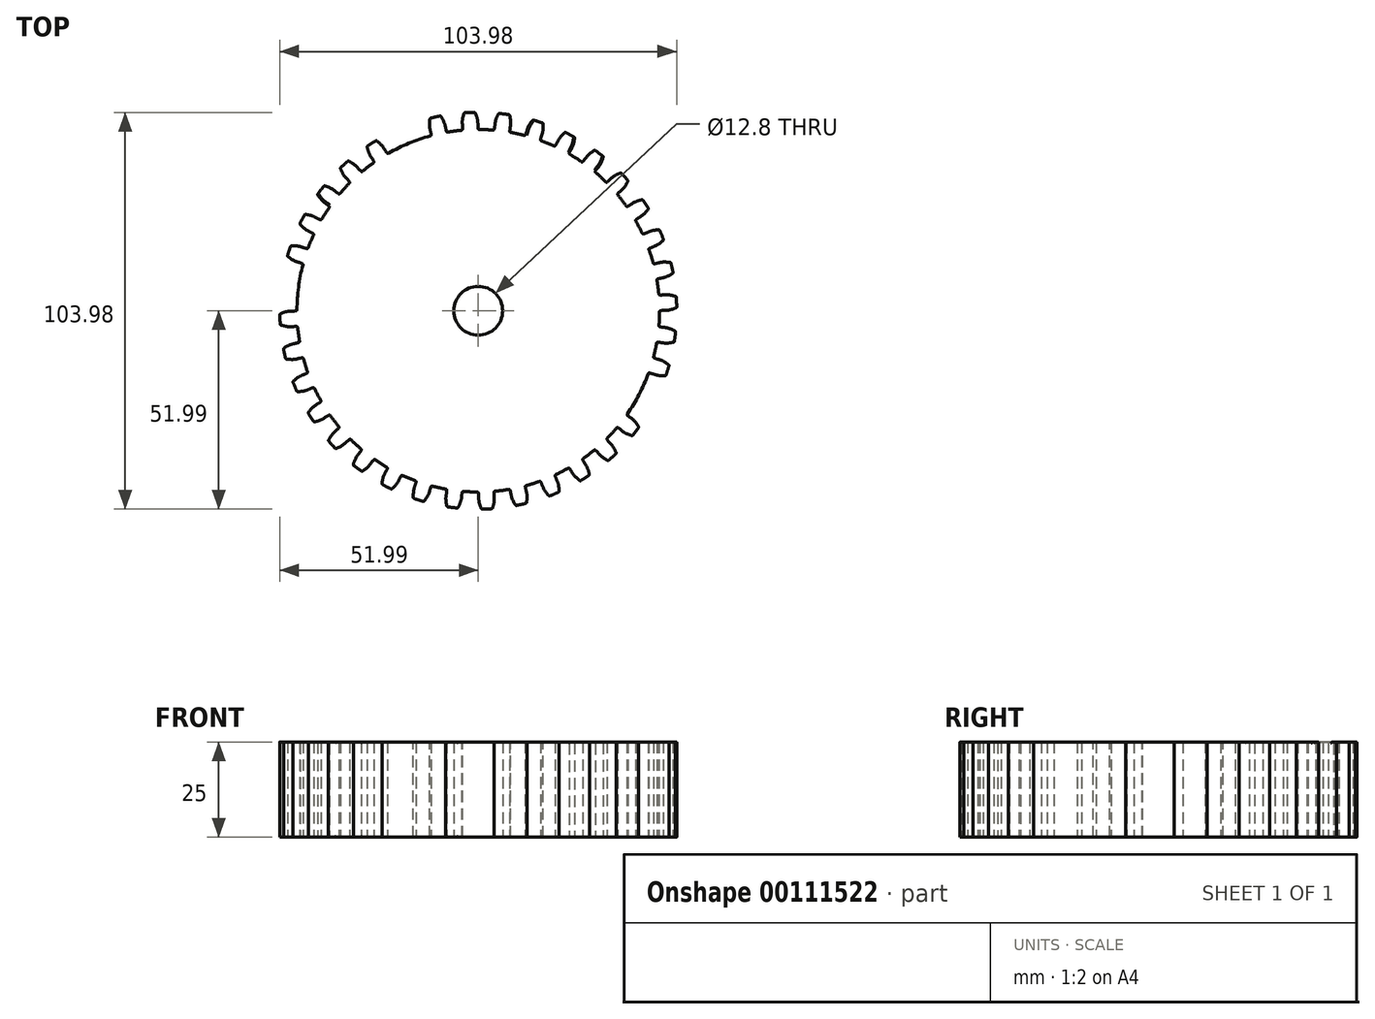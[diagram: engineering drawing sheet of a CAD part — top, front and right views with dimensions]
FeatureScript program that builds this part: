
annotation { "Feature Type Name" : "Feature", "Feature Type Description" : "" }
export const myFeature = defineFeature(function(context is Context, id is Id, definition is map)
    precondition{}
    {
        {
            var Q0;
            Q0=qCreatedBy(makeId("Top.planeOp"),FACE);
            var sketch = newSketch(context, id + "F0", { "sketchPlane" : qUnion([Q0])});
            skCircle(sketch, "E0", {"center": v(0, 0) * mm, "radius": 47.5 * mm});
            skCircle(sketch, "E1", {"center": v(0, 0) * mm, "radius": 52 * mm});
            skFitSpline(sketch, "E2", {"points": [v(-0.54, 52) * mm, v(0, 50) * mm, v(0.28, 47.5) * mm], "startDerivative": vector(1.25, -3.55) * mm, "endDerivative": vector(0.53, -5.13) * mm});
            skFitSpline(sketch, "E3.MirrorCS", {"points": [v(0.54, 52) * mm, v(0, 50) * mm, v(-0.28, 47.5) * mm], "startDerivative": vector(-1.25, -3.55) * mm, "endDerivative": vector(-0.53, -5.13) * mm});
            skFitSpline(sketch, "E4.0", {"points": [v(-0.54, 52) * mm, v(-0.34, 51.43) * mm, v(0.1, 49.94) * mm, v(0.19, 48.4) * mm, v(0.28, 47.5) * mm]});
            skFitSpline(sketch, "E5.0", {"points": [v(-0.82, 52) * mm, v(-0.62, 51.44) * mm, v(-0.18, 49.94) * mm, v(-0.1, 48.4) * mm, v(0, 47.5) * mm]});
            skCircle(sketch, "E6.3.0", {"center": v(0, 0) * mm, "radius": 73.48 * mm});
            skCircle(sketch, "E6.4.0", {"center": v(0, 0) * mm, "radius": 73.48 * mm});
            skCircle(sketch, "E6.6.0", {"center": v(0, 0) * mm, "radius": 73.48 * mm});
            skCircle(sketch, "E6.7.0", {"center": v(0, 0) * mm, "radius": 73.48 * mm});
            skCircle(sketch, "E6.8.0", {"center": v(0, 0) * mm, "radius": 73.48 * mm});
            skCircle(sketch, "E6.9.0", {"center": v(0, 0) * mm, "radius": 73.48 * mm});
            skCircle(sketch, "E6.10.0", {"center": v(0, 0) * mm, "radius": 73.48 * mm});
            skCircle(sketch, "E6.11.0", {"center": v(0, 0) * mm, "radius": 73.48 * mm});
            skCircle(sketch, "E6.12.0", {"center": v(0, 0) * mm, "radius": 73.48 * mm});
            skCircle(sketch, "E6.13.0", {"center": v(0, 0) * mm, "radius": 73.48 * mm});
            skCircle(sketch, "E6.14.0", {"center": v(0, 0) * mm, "radius": 73.48 * mm});
            skCircle(sketch, "E6.15.0", {"center": v(0, 0) * mm, "radius": 73.48 * mm});
            skCircle(sketch, "E6.16.0", {"center": v(0, 0) * mm, "radius": 73.48 * mm});
            skCircle(sketch, "E6.17.0", {"center": v(0, 0) * mm, "radius": 73.48 * mm});
            skCircle(sketch, "E6.18.0", {"center": v(0, 0) * mm, "radius": 73.48 * mm});
            skCircle(sketch, "E6.19.0", {"center": v(0, 0) * mm, "radius": 73.48 * mm});
            skCircle(sketch, "E6.20.0", {"center": v(0, 0) * mm, "radius": 73.48 * mm});
            skCircle(sketch, "E6.21.0", {"center": v(0, 0) * mm, "radius": 73.48 * mm});
            skCircle(sketch, "E6.22.0", {"center": v(0, 0) * mm, "radius": 73.48 * mm});
            skCircle(sketch, "E6.23.0", {"center": v(0, 0) * mm, "radius": 73.48 * mm});
            skCircle(sketch, "E6.24.0", {"center": v(0, 0) * mm, "radius": 73.48 * mm});
            skCircle(sketch, "E6.26.0", {"center": v(0, 0) * mm, "radius": 73.48 * mm});
            skCircle(sketch, "E6.27.0", {"center": v(0, 0) * mm, "radius": 73.48 * mm});
            skCircle(sketch, "E6.28.0", {"center": v(0, 0) * mm, "radius": 73.48 * mm});
            skCircle(sketch, "E6.29.0", {"center": v(0, 0) * mm, "radius": 73.48 * mm});
            skCircle(sketch, "E6.30.0", {"center": v(0, 0) * mm, "radius": 73.48 * mm});
            skCircle(sketch, "E6.31.0", {"center": v(0, 0) * mm, "radius": 73.48 * mm});
            skCircle(sketch, "E6.32.0", {"center": v(0, 0) * mm, "radius": 73.48 * mm});
            skCircle(sketch, "E6.33.0", {"center": v(0, 0) * mm, "radius": 73.48 * mm});
            skCircle(sketch, "E6.34.0", {"center": v(0, 0) * mm, "radius": 73.48 * mm});
            skCircle(sketch, "E6.35.0", {"center": v(0, 0) * mm, "radius": 73.48 * mm});
            skCircle(sketch, "E6.36.0", {"center": v(0, 0) * mm, "radius": 73.48 * mm});
            skCircle(sketch, "E6.38.0", {"center": v(0, 0) * mm, "radius": 73.48 * mm});
            skCircle(sketch, "E6.39.0", {"center": v(0, 0) * mm, "radius": 73.48 * mm});
            skCircle(sketch, "E6.40.0", {"center": v(0, 0) * mm, "radius": 73.48 * mm});
            skCircle(sketch, "E6.41.0", {"center": v(0, 0) * mm, "radius": 73.48 * mm});
            skCircle(sketch, "E6.42.0", {"center": v(0, 0) * mm, "radius": 73.48 * mm});
            skCircle(sketch, "E6.43.0", {"center": v(0, 0) * mm, "radius": 73.48 * mm});
            skCircle(sketch, "E6.44.0", {"center": v(0, 0) * mm, "radius": 73.48 * mm});
            skCircle(sketch, "E6.45.0", {"center": v(0, 0) * mm, "radius": 73.48 * mm});
            skCircle(sketch, "E6.46.0", {"center": v(0, 0) * mm, "radius": 73.48 * mm});
            skCircle(sketch, "E6.47.0", {"center": v(0, 0) * mm, "radius": 73.48 * mm});
            skCircle(sketch, "E6.49.0", {"center": v(0, 0) * mm, "radius": 73.48 * mm});
            skCircle(sketch, "E6.50.0", {"center": v(0, 0) * mm, "radius": 73.48 * mm});
            skCircle(sketch, "E6.52.0", {"center": v(0, 0) * mm, "radius": 73.48 * mm});
            skCircle(sketch, "E6.53.0", {"center": v(0, 0) * mm, "radius": 73.48 * mm});
            skCircle(sketch, "E6.54.0", {"center": v(0, 0) * mm, "radius": 73.48 * mm});
            skCircle(sketch, "E6.55.0", {"center": v(0, 0) * mm, "radius": 73.48 * mm});
            skCircle(sketch, "E6.56.0", {"center": v(0, 0) * mm, "radius": 73.48 * mm});
            skCircle(sketch, "E6.57.0", {"center": v(0, 0) * mm, "radius": 73.48 * mm});
            skCircle(sketch, "E6.58.0", {"center": v(0, 0) * mm, "radius": 73.48 * mm});
            skCircle(sketch, "E6.59.0", {"center": v(0, 0) * mm, "radius": 73.48 * mm});
            skCircle(sketch, "E6.60.0", {"center": v(0, 0) * mm, "radius": 73.48 * mm});
            skCircle(sketch, "E6.61.0", {"center": v(0, 0) * mm, "radius": 73.48 * mm});
            skCircle(sketch, "E6.62.0", {"center": v(0, 0) * mm, "radius": 73.48 * mm});
            skCircle(sketch, "E6.63.0", {"center": v(0, 0) * mm, "radius": 73.48 * mm});
            skCircle(sketch, "E6.64.0", {"center": v(0, 0) * mm, "radius": 73.48 * mm});
            skCircle(sketch, "E6.65.0", {"center": v(0, 0) * mm, "radius": 73.48 * mm});
            skCircle(sketch, "E6.66.0", {"center": v(0, 0) * mm, "radius": 73.48 * mm});
            skCircle(sketch, "E6.67.0", {"center": v(0, 0) * mm, "radius": 73.48 * mm});
            skCircle(sketch, "E6.68.0", {"center": v(0, 0) * mm, "radius": 73.48 * mm});
            skCircle(sketch, "E6.69.0", {"center": v(0, 0) * mm, "radius": 73.48 * mm});
            skCircle(sketch, "E6.70.0", {"center": v(0, 0) * mm, "radius": 73.48 * mm});
            skCircle(sketch, "E6.71.0", {"center": v(0, 0) * mm, "radius": 73.48 * mm});
            skCircle(sketch, "E6.72.0", {"center": v(0, 0) * mm, "radius": 73.48 * mm});
            skCircle(sketch, "E6.73.0", {"center": v(0, 0) * mm, "radius": 73.48 * mm});
            skCircle(sketch, "E6.74.0", {"center": v(0, 0) * mm, "radius": 73.48 * mm});
            skCircle(sketch, "E6.75.0", {"center": v(0, 0) * mm, "radius": 73.48 * mm});
            skCircle(sketch, "E6.76.0", {"center": v(0, 0) * mm, "radius": 73.48 * mm});
            skCircle(sketch, "E6.77.0", {"center": v(0, 0) * mm, "radius": 73.48 * mm});
            skCircle(sketch, "E6.78.0", {"center": v(0, 0) * mm, "radius": 73.48 * mm});
            skCircle(sketch, "E6.79.0", {"center": v(0, 0) * mm, "radius": 73.48 * mm});
            skCircle(sketch, "E6.80.0", {"center": v(0, 0) * mm, "radius": 73.48 * mm});
            skCircle(sketch, "E6.81.0", {"center": v(0, 0) * mm, "radius": 73.48 * mm});
            skCircle(sketch, "E6.82.0", {"center": v(0, 0) * mm, "radius": 73.48 * mm});
            skCircle(sketch, "E6.83.0", {"center": v(0, 0) * mm, "radius": 73.48 * mm});
            skCircle(sketch, "E6.84.0", {"center": v(0, 0) * mm, "radius": 73.48 * mm});
            skCircle(sketch, "E6.85.0", {"center": v(0, 0) * mm, "radius": 73.48 * mm});
            skCircle(sketch, "E6.86.0", {"center": v(0, 0) * mm, "radius": 73.48 * mm});
            skCircle(sketch, "E6.87.0", {"center": v(0, 0) * mm, "radius": 73.48 * mm});
            skCircle(sketch, "E6.88.0", {"center": v(0, 0) * mm, "radius": 73.48 * mm});
            skCircle(sketch, "E6.89.0", {"center": v(0, 0) * mm, "radius": 73.48 * mm});
            skCircle(sketch, "E6.90.0", {"center": v(0, 0) * mm, "radius": 73.48 * mm});
            skCircle(sketch, "E6.91.0", {"center": v(0, 0) * mm, "radius": 73.48 * mm});
            skCircle(sketch, "E6.92.0", {"center": v(0, 0) * mm, "radius": 73.48 * mm});
            skCircle(sketch, "E6.93.0", {"center": v(0, 0) * mm, "radius": 73.48 * mm});
            skCircle(sketch, "E6.94.0", {"center": v(0, 0) * mm, "radius": 73.48 * mm});
            skCircle(sketch, "E6.95.0", {"center": v(0, 0) * mm, "radius": 73.48 * mm});
            skCircle(sketch, "E6.96.0", {"center": v(0, 0) * mm, "radius": 73.48 * mm});
            skCircle(sketch, "E6.97.0", {"center": v(0, 0) * mm, "radius": 73.48 * mm});
            skCircle(sketch, "E6.98.0", {"center": v(0, 0) * mm, "radius": 73.48 * mm});
            skCircle(sketch, "E6.99.0", {"center": v(0, 0) * mm, "radius": 73.48 * mm});
            skCircle(sketch, "E6.100.0", {"center": v(0, 0) * mm, "radius": 73.48 * mm});
            skCircle(sketch, "E6.101.0", {"center": v(0, 0) * mm, "radius": 73.48 * mm});
            skCircle(sketch, "E6.102.0", {"center": v(0, 0) * mm, "radius": 73.48 * mm});
            skCircle(sketch, "E6.103.0", {"center": v(0, 0) * mm, "radius": 73.48 * mm});
            skCircle(sketch, "E6.104.0", {"center": v(0, 0) * mm, "radius": 73.48 * mm});
            skCircle(sketch, "E6.105.0", {"center": v(0, 0) * mm, "radius": 73.48 * mm});
            skCircle(sketch, "E6.106.0", {"center": v(0, 0) * mm, "radius": 73.48 * mm});
            skCircle(sketch, "E6.109.0", {"center": v(0, 0) * mm, "radius": 73.48 * mm});
            skCircle(sketch, "E6.113.0", {"center": v(0, 0) * mm, "radius": 73.48 * mm});
            skCircle(sketch, "E6.114.0", {"center": v(0, 0) * mm, "radius": 73.48 * mm});
            skCircle(sketch, "E6.115.0", {"center": v(0, 0) * mm, "radius": 73.48 * mm});
            skCircle(sketch, "E6.116.0", {"center": v(0, 0) * mm, "radius": 73.48 * mm});
            skCircle(sketch, "E6.117.0", {"center": v(0, 0) * mm, "radius": 73.48 * mm});
            skCircle(sketch, "E6.118.0", {"center": v(0, 0) * mm, "radius": 73.48 * mm});
            skCircle(sketch, "E6.119.0", {"center": v(0, 0) * mm, "radius": 73.48 * mm});
            skCircle(sketch, "E6.120.0", {"center": v(0, 0) * mm, "radius": 73.48 * mm});
            skCircle(sketch, "E6.123.0", {"center": v(0, 0) * mm, "radius": 73.48 * mm});
            skCircle(sketch, "E6.124.0", {"center": v(0, 0) * mm, "radius": 73.48 * mm});
            skCircle(sketch, "E6.125.0", {"center": v(0, 0) * mm, "radius": 73.48 * mm});
            skCircle(sketch, "E6.126.0", {"center": v(0, 0) * mm, "radius": 73.48 * mm});
            skCircle(sketch, "E6.127.0", {"center": v(0, 0) * mm, "radius": 73.48 * mm});
            skCircle(sketch, "E6.128.0", {"center": v(0, 0) * mm, "radius": 73.48 * mm});
            skCircle(sketch, "E6.130.0", {"center": v(0, 0) * mm, "radius": 73.48 * mm});
            skCircle(sketch, "E6.134.0", {"center": v(0, 0) * mm, "radius": 73.48 * mm});
            skCircle(sketch, "E6.135.0", {"center": v(0, 0) * mm, "radius": 73.48 * mm});
            skCircle(sketch, "E6.137.0", {"center": v(0, 0) * mm, "radius": 73.48 * mm});
            skCircle(sketch, "E6.138.0", {"center": v(0, 0) * mm, "radius": 73.48 * mm});
            skCircle(sketch, "E6.139.0", {"center": v(0, 0) * mm, "radius": 73.48 * mm});
            skCircle(sketch, "E6.140.0", {"center": v(0, 0) * mm, "radius": 73.48 * mm});
            skCircle(sketch, "E6.141.0", {"center": v(0, 0) * mm, "radius": 73.48 * mm});
            skCircle(sketch, "E6.142.0", {"center": v(0, 0) * mm, "radius": 73.48 * mm});
            skCircle(sketch, "E6.143.0", {"center": v(0, 0) * mm, "radius": 73.48 * mm});
            skFitSpline(sketch, "E7.MirrorCS", {"points": [v(-3.72, 51.87) * mm, v(-3.86, 51.3) * mm, v(-4.18, 49.76) * mm, v(-4.13, 48.22) * mm, v(-4.14, 47.32) * mm]});
            skFitSpline(sketch, "E8.MirrorCS", {"points": [v(-3.72, 51.87) * mm, v(-3.86, 51.3) * mm, v(-4.18, 49.76) * mm, v(-4.13, 48.22) * mm, v(-4.14, 47.32) * mm]});
            skFitSpline(sketch, "E9.MirrorCS", {"points": [v(-3.72, 51.87) * mm, v(-3.86, 51.3) * mm, v(-4.18, 49.76) * mm, v(-4.13, 48.22) * mm, v(-4.14, 47.32) * mm]});
            skFitSpline(sketch, "E10.MirrorCS", {"points": [v(-3.72, 51.87) * mm, v(-3.86, 51.3) * mm, v(-4.18, 49.76) * mm, v(-4.13, 48.22) * mm, v(-4.14, 47.32) * mm]});
            skFitSpline(sketch, "E11.MirrorCS", {"points": [v(-9.84, 51.07) * mm, v(-9.54, 50.55) * mm, v(-8.85, 49.15) * mm, v(-8.5, 47.64) * mm, v(-8.25, 46.78) * mm]});
            skFitSpline(sketch, "E12.MirrorCS", {"points": [v(-12.67, 50.44) * mm, v(-12.71, 49.84) * mm, v(-12.75, 48.28) * mm, v(-12.44, 46.77) * mm, v(-12.3, 45.88) * mm]});
            skFitSpline(sketch, "E13.MirrorCS", {"points": [v(-18.55, 48.58) * mm, v(-18.18, 48.12) * mm, v(-17.25, 46.86) * mm, v(-16.64, 45.45) * mm, v(-16.25, 44.64) * mm]});
            skFitSpline(sketch, "E14.MirrorCS", {"points": [v(-18.55, 48.58) * mm, v(-18.18, 48.12) * mm, v(-17.25, 46.86) * mm, v(-16.64, 45.45) * mm, v(-16.25, 44.64) * mm]});
            skFitSpline(sketch, "E15.MirrorCS", {"points": [v(-21.23, 47.47) * mm, v(-21.17, 46.88) * mm, v(-20.94, 45.33) * mm, v(-20.37, 43.9) * mm, v(-20.07, 43.05) * mm]});
            skFitSpline(sketch, "E16.MirrorCS", {"points": [v(-26.7, 44.62) * mm, v(-26.26, 44.23) * mm, v(-25.12, 43.16) * mm, v(-24.28, 41.87) * mm, v(-23.75, 41.14) * mm]});
            skFitSpline(sketch, "E17.MirrorCS", {"points": [v(-29.15, 43.06) * mm, v(-29, 42.5) * mm, v(-28.5, 41) * mm, v(-27.68, 39.7) * mm, v(-27.24, 38.91) * mm]});
            skFitSpline(sketch, "E18.MirrorCS", {"points": [v(-34.05, 39.3) * mm, v(-33.54, 39) * mm, v(-32.23, 38.14) * mm, v(-31.18, 37.01) * mm, v(-30.53, 36.39) * mm]});
            skFitSpline(sketch, "E19.MirrorCS", {"points": [v(-36.19, 37.35) * mm, v(-35.93, 36.81) * mm, v(-35.19, 35.44) * mm, v(-34.16, 34.29) * mm, v(-33.59, 33.59) * mm]});
            skFitSpline(sketch, "E20.MirrorCS", {"points": [v(-40.36, 32.8) * mm, v(-39.8, 32.59) * mm, v(-38.37, 31.96) * mm, v(-37.13, 31.04) * mm, v(-36.39, 30.53) * mm]});
            skFitSpline(sketch, "E21.MirrorCS", {"points": [v(-42.12, 30.5) * mm, v(-41.78, 30.01) * mm, v(-40.8, 28.79) * mm, v(-39.6, 27.83) * mm, v(-38.9, 27.25) * mm]});
            skFitSpline(sketch, "E22.MirrorCS", {"points": [v(-45.44, 25.29) * mm, v(-44.86, 25.18) * mm, v(-43.34, 24.81) * mm, v(-41.96, 24.12) * mm, v(-41.14, 23.75) * mm]});
            skFitSpline(sketch, "E23.MirrorCS", {"points": [v(-46.78, 22.72) * mm, v(-46.35, 22.3) * mm, v(-45.18, 21.26) * mm, v(-43.82, 20.54) * mm, v(-43.05, 20.08) * mm]});
            skFitSpline(sketch, "E24.MirrorCS", {"points": [v(-49.14, 17.01) * mm, v(-48.55, 17) * mm, v(-46.99, 16.91) * mm, v(-45.5, 16.47) * mm, v(-44.64, 16.25) * mm]});
            skFitSpline(sketch, "E25.MirrorCS", {"points": [v(-50.01, 14.25) * mm, v(-49.52, 13.91) * mm, v(-48.19, 13.1) * mm, v(-46.72, 12.62) * mm, v(-45.88, 12.3) * mm]});
            skFitSpline(sketch, "E26.MirrorCS", {"points": [v(-51.35, 8.22) * mm, v(-50.76, 8.32) * mm, v(-49.2, 8.5) * mm, v(-47.68, 8.31) * mm, v(-46.78, 8.25) * mm]});
            skFitSpline(sketch, "E27.MirrorCS", {"points": [v(-51.35, 8.22) * mm, v(-50.76, 8.32) * mm, v(-49.2, 8.5) * mm, v(-47.68, 8.31) * mm, v(-46.78, 8.25) * mm]});
            skFitSpline(sketch, "E28.MirrorCS", {"points": [v(-51.73, 5.35) * mm, v(-51.19, 5.1) * mm, v(-49.73, 4.53) * mm, v(-48.2, 4.31) * mm, v(-47.32, 4.14) * mm]});
            skFitSpline(sketch, "E29.MirrorCS", {"points": [v(-52, -0.82) * mm, v(-51.44, -0.62) * mm, v(-49.94, -0.18) * mm, v(-48.4, -0.1) * mm, v(-47.5, 0) * mm]});
            skFitSpline(sketch, "E30.MirrorCS", {"points": [v(-51.87, -3.72) * mm, v(-51.3, -3.86) * mm, v(-49.76, -4.18) * mm, v(-48.22, -4.13) * mm, v(-47.32, -4.14) * mm]});
            skFitSpline(sketch, "E31.MirrorCS", {"points": [v(-51.07, -9.84) * mm, v(-50.55, -9.54) * mm, v(-49.15, -8.85) * mm, v(-47.64, -8.5) * mm, v(-46.78, -8.25) * mm]});
            skFitSpline(sketch, "E32.MirrorCS", {"points": [v(-50.44, -12.67) * mm, v(-49.84, -12.71) * mm, v(-48.28, -12.75) * mm, v(-46.77, -12.44) * mm, v(-45.88, -12.3) * mm]});
            skFitSpline(sketch, "E33.MirrorCS", {"points": [v(-48.58, -18.55) * mm, v(-48.12, -18.18) * mm, v(-46.86, -17.25) * mm, v(-45.45, -16.64) * mm, v(-44.64, -16.25) * mm]});
            skFitSpline(sketch, "E34.MirrorCS", {"points": [v(-47.47, -21.23) * mm, v(-46.88, -21.17) * mm, v(-45.33, -20.94) * mm, v(-43.9, -20.37) * mm, v(-43.05, -20.07) * mm]});
            skFitSpline(sketch, "E35.MirrorCS", {"points": [v(-44.62, -26.7) * mm, v(-44.23, -26.26) * mm, v(-43.16, -25.12) * mm, v(-41.87, -24.28) * mm, v(-41.14, -23.75) * mm]});
            skFitSpline(sketch, "E36.MirrorCS", {"points": [v(-43.06, -29.15) * mm, v(-42.5, -29) * mm, v(-41, -28.5) * mm, v(-39.7, -27.68) * mm, v(-38.91, -27.24) * mm]});
            skFitSpline(sketch, "E37.MirrorCS", {"points": [v(-39.3, -34.05) * mm, v(-39, -33.54) * mm, v(-38.14, -32.23) * mm, v(-37.01, -31.18) * mm, v(-36.39, -30.53) * mm]});
            skFitSpline(sketch, "E38.MirrorCS", {"points": [v(-37.35, -36.19) * mm, v(-36.81, -35.93) * mm, v(-35.44, -35.19) * mm, v(-34.29, -34.16) * mm, v(-33.59, -33.59) * mm]});
            skFitSpline(sketch, "E39.MirrorCS", {"points": [v(-32.8, -40.36) * mm, v(-32.59, -39.8) * mm, v(-31.96, -38.37) * mm, v(-31.04, -37.13) * mm, v(-30.53, -36.39) * mm]});
            skFitSpline(sketch, "E40.MirrorCS", {"points": [v(-30.5, -42.12) * mm, v(-30.01, -41.78) * mm, v(-28.79, -40.8) * mm, v(-27.83, -39.6) * mm, v(-27.25, -38.9) * mm]});
            skFitSpline(sketch, "E41.MirrorCS", {"points": [v(-25.29, -45.44) * mm, v(-25.18, -44.86) * mm, v(-24.81, -43.34) * mm, v(-24.12, -41.96) * mm, v(-23.75, -41.14) * mm]});
            skFitSpline(sketch, "E42.MirrorCS", {"points": [v(-22.72, -46.78) * mm, v(-22.3, -46.35) * mm, v(-21.26, -45.18) * mm, v(-20.54, -43.82) * mm, v(-20.08, -43.05) * mm]});
            skFitSpline(sketch, "E43.MirrorCS", {"points": [v(-17.01, -49.14) * mm, v(-17, -48.55) * mm, v(-16.91, -46.99) * mm, v(-16.47, -45.5) * mm, v(-16.25, -44.64) * mm]});
            skFitSpline(sketch, "E44.MirrorCS", {"points": [v(-14.25, -50.01) * mm, v(-13.91, -49.52) * mm, v(-13.1, -48.19) * mm, v(-12.62, -46.72) * mm, v(-12.3, -45.88) * mm]});
            skFitSpline(sketch, "E45.MirrorCS", {"points": [v(-8.22, -51.35) * mm, v(-8.32, -50.76) * mm, v(-8.5, -49.2) * mm, v(-8.31, -47.68) * mm, v(-8.25, -46.78) * mm]});
            skFitSpline(sketch, "E46.MirrorCS", {"points": [v(-5.35, -51.73) * mm, v(-5.1, -51.19) * mm, v(-4.53, -49.73) * mm, v(-4.31, -48.2) * mm, v(-4.14, -47.32) * mm]});
            skFitSpline(sketch, "E47.MirrorCS", {"points": [v(0.82, -52) * mm, v(0.62, -51.44) * mm, v(0.18, -49.94) * mm, v(0.1, -48.4) * mm, v(0, -47.5) * mm]});
            skFitSpline(sketch, "E48.MirrorCS", {"points": [v(3.72, -51.87) * mm, v(3.86, -51.3) * mm, v(4.18, -49.76) * mm, v(4.13, -48.22) * mm, v(4.14, -47.32) * mm]});
            skFitSpline(sketch, "E49.MirrorCS", {"points": [v(3.72, -51.87) * mm, v(3.86, -51.3) * mm, v(4.18, -49.76) * mm, v(4.13, -48.22) * mm, v(4.14, -47.32) * mm]});
            skFitSpline(sketch, "E50.MirrorCS", {"points": [v(9.84, -51.07) * mm, v(9.54, -50.55) * mm, v(8.85, -49.15) * mm, v(8.5, -47.64) * mm, v(8.25, -46.78) * mm]});
            skFitSpline(sketch, "E51.MirrorCS", {"points": [v(12.67, -50.44) * mm, v(12.71, -49.84) * mm, v(12.75, -48.28) * mm, v(12.44, -46.77) * mm, v(12.3, -45.88) * mm]});
            skFitSpline(sketch, "E52.MirrorCS", {"points": [v(18.55, -48.58) * mm, v(18.18, -48.12) * mm, v(17.25, -46.86) * mm, v(16.64, -45.45) * mm, v(16.25, -44.64) * mm]});
            skFitSpline(sketch, "E53.MirrorCS", {"points": [v(21.23, -47.47) * mm, v(21.17, -46.88) * mm, v(20.94, -45.33) * mm, v(20.37, -43.9) * mm, v(20.07, -43.05) * mm]});
            skFitSpline(sketch, "E54.MirrorCS", {"points": [v(26.7, -44.62) * mm, v(26.26, -44.23) * mm, v(25.12, -43.16) * mm, v(24.28, -41.87) * mm, v(23.75, -41.14) * mm]});
            skFitSpline(sketch, "E55.MirrorCS", {"points": [v(29.15, -43.06) * mm, v(29, -42.5) * mm, v(28.5, -41) * mm, v(27.68, -39.7) * mm, v(27.24, -38.91) * mm]});
            skFitSpline(sketch, "E56.MirrorCS", {"points": [v(34.05, -39.3) * mm, v(33.54, -39) * mm, v(32.23, -38.14) * mm, v(31.18, -37.01) * mm, v(30.53, -36.39) * mm]});
            skFitSpline(sketch, "E57.MirrorCS", {"points": [v(36.19, -37.35) * mm, v(35.93, -36.81) * mm, v(35.19, -35.44) * mm, v(34.16, -34.29) * mm, v(33.59, -33.59) * mm]});
            skFitSpline(sketch, "E58.MirrorCS", {"points": [v(40.36, -32.8) * mm, v(39.8, -32.59) * mm, v(38.37, -31.96) * mm, v(37.13, -31.04) * mm, v(36.39, -30.53) * mm]});
            skFitSpline(sketch, "E59.MirrorCS", {"points": [v(42.12, -30.5) * mm, v(41.78, -30.01) * mm, v(40.8, -28.79) * mm, v(39.6, -27.83) * mm, v(38.9, -27.25) * mm]});
            skFitSpline(sketch, "E60.MirrorCS", {"points": [v(45.44, -25.29) * mm, v(44.86, -25.18) * mm, v(43.34, -24.81) * mm, v(41.96, -24.12) * mm, v(41.14, -23.75) * mm]});
            skFitSpline(sketch, "E61.MirrorCS", {"points": [v(45.44, -25.29) * mm, v(44.86, -25.18) * mm, v(43.34, -24.81) * mm, v(41.96, -24.12) * mm, v(41.14, -23.75) * mm]});
            skFitSpline(sketch, "E62.MirrorCS", {"points": [v(46.78, -22.72) * mm, v(46.35, -22.3) * mm, v(45.18, -21.26) * mm, v(43.82, -20.54) * mm, v(43.05, -20.08) * mm]});
            skFitSpline(sketch, "E63.MirrorCS", {"points": [v(49.14, -17.01) * mm, v(48.55, -17) * mm, v(46.99, -16.91) * mm, v(45.5, -16.47) * mm, v(44.64, -16.25) * mm]});
            skFitSpline(sketch, "E64.MirrorCS", {"points": [v(50.01, -14.25) * mm, v(49.52, -13.91) * mm, v(48.19, -13.1) * mm, v(46.72, -12.62) * mm, v(45.88, -12.3) * mm]});
            skFitSpline(sketch, "E65.MirrorCS", {"points": [v(51.35, -8.22) * mm, v(50.76, -8.32) * mm, v(49.2, -8.5) * mm, v(47.68, -8.31) * mm, v(46.78, -8.25) * mm]});
            skFitSpline(sketch, "E66.MirrorCS", {"points": [v(51.73, -5.35) * mm, v(51.19, -5.1) * mm, v(49.73, -4.53) * mm, v(48.2, -4.31) * mm, v(47.32, -4.14) * mm]});
            skFitSpline(sketch, "E67.MirrorCS", {"points": [v(52, 0.82) * mm, v(51.44, 0.62) * mm, v(49.94, 0.18) * mm, v(48.4, 0.1) * mm, v(47.5, 0) * mm]});
            skFitSpline(sketch, "E68.MirrorCS", {"points": [v(51.87, 3.72) * mm, v(51.3, 3.86) * mm, v(49.76, 4.18) * mm, v(48.22, 4.13) * mm, v(47.32, 4.14) * mm]});
            skFitSpline(sketch, "E69.MirrorCS", {"points": [v(51.07, 9.84) * mm, v(50.55, 9.54) * mm, v(49.15, 8.85) * mm, v(47.64, 8.5) * mm, v(46.78, 8.25) * mm]});
            skFitSpline(sketch, "E70.MirrorCS", {"points": [v(50.44, 12.67) * mm, v(49.84, 12.71) * mm, v(48.28, 12.75) * mm, v(46.77, 12.44) * mm, v(45.88, 12.3) * mm]});
            skFitSpline(sketch, "E71.MirrorCS", {"points": [v(48.58, 18.55) * mm, v(48.12, 18.18) * mm, v(46.86, 17.25) * mm, v(45.45, 16.64) * mm, v(44.64, 16.25) * mm]});
            skFitSpline(sketch, "E72.MirrorCS", {"points": [v(47.47, 21.23) * mm, v(46.88, 21.17) * mm, v(45.33, 20.94) * mm, v(43.9, 20.37) * mm, v(43.05, 20.07) * mm]});
            skFitSpline(sketch, "E73.MirrorCS", {"points": [v(44.62, 26.7) * mm, v(44.23, 26.26) * mm, v(43.16, 25.12) * mm, v(41.87, 24.28) * mm, v(41.14, 23.75) * mm]});
            skFitSpline(sketch, "E74.MirrorCS", {"points": [v(43.06, 29.15) * mm, v(42.5, 29) * mm, v(41, 28.5) * mm, v(39.7, 27.68) * mm, v(38.91, 27.24) * mm]});
            skFitSpline(sketch, "E75.MirrorCS", {"points": [v(39.3, 34.05) * mm, v(39, 33.54) * mm, v(38.14, 32.23) * mm, v(37.01, 31.18) * mm, v(36.39, 30.53) * mm]});
            skFitSpline(sketch, "E76.MirrorCS", {"points": [v(37.35, 36.19) * mm, v(36.81, 35.93) * mm, v(35.44, 35.19) * mm, v(34.29, 34.16) * mm, v(33.59, 33.59) * mm]});
            skFitSpline(sketch, "E77.MirrorCS", {"points": [v(32.8, 40.36) * mm, v(32.59, 39.8) * mm, v(31.96, 38.37) * mm, v(31.04, 37.13) * mm, v(30.53, 36.39) * mm]});
            skFitSpline(sketch, "E78.MirrorCS", {"points": [v(30.5, 42.12) * mm, v(30.01, 41.78) * mm, v(28.79, 40.8) * mm, v(27.83, 39.6) * mm, v(27.25, 38.9) * mm]});
            skFitSpline(sketch, "E79.MirrorCS", {"points": [v(25.29, 45.44) * mm, v(25.18, 44.86) * mm, v(24.81, 43.34) * mm, v(24.12, 41.96) * mm, v(23.75, 41.14) * mm]});
            skFitSpline(sketch, "E80.MirrorCS", {"points": [v(22.72, 46.78) * mm, v(22.3, 46.35) * mm, v(21.26, 45.18) * mm, v(20.54, 43.82) * mm, v(20.08, 43.05) * mm]});
            skFitSpline(sketch, "E81.MirrorCS", {"points": [v(17.01, 49.14) * mm, v(17, 48.55) * mm, v(16.91, 46.99) * mm, v(16.47, 45.5) * mm, v(16.25, 44.64) * mm]});
            skFitSpline(sketch, "E82.MirrorCS", {"points": [v(14.25, 50.01) * mm, v(13.91, 49.52) * mm, v(13.1, 48.19) * mm, v(12.62, 46.72) * mm, v(12.3, 45.88) * mm]});
            skFitSpline(sketch, "E83.MirrorCS", {"points": [v(8.22, 51.35) * mm, v(8.32, 50.76) * mm, v(8.5, 49.2) * mm, v(8.31, 47.68) * mm, v(8.25, 46.78) * mm]});
            skFitSpline(sketch, "E84.MirrorCS", {"points": [v(5.35, 51.73) * mm, v(5.1, 51.19) * mm, v(4.53, 49.73) * mm, v(4.31, 48.2) * mm, v(4.14, 47.32) * mm]});
            skFitSpline(sketch, "E85.MirrorCS", {"points": [v(-0.82, 52) * mm, v(-0.62, 51.44) * mm, v(-0.18, 49.94) * mm, v(-0.1, 48.4) * mm, v(0, 47.5) * mm]});
            skCircle(sketch, "E86", {"center": v(0, 0) * mm, "radius": 6.4 * mm});
            skSolve(sketch);
        }
        {
            var Q0;
            {var subQ0=sQuery(id+"F0.wireOp",EDGE,"E0");var subQ35=makeQuery(id+"F0.imprint","INTERSECT",VERTEX,{"derivedFrom":[subQ0,sQuery(id+"F0.wireOp",EDGE,"E67.MirrorCS")]});Q0=makeQuery(id+"F0.imprint","IMPRINT",FACE,{"disambiguationData":[TD([[makeQuery(id+"F0.imprint","IMPRINT",EDGE,{"disambiguationData":[TD([[subQ35,-1.0]])],"derivedFrom":subQ0}),1.0]])]});}
            var Q1;
            {var subQ0=sQuery(id+"F0.wireOp",EDGE,"E22.MirrorCS");var subQ1=sQuery(id+"F0.wireOp",EDGE,"E0");var subQ2=makeQuery(id+"F0.imprint","INTERSECT",VERTEX,{"derivedFrom":[subQ1,subQ0]});Q1=makeQuery(id+"F0.imprint","IMPRINT",FACE,{"disambiguationData":[TD([[makeQuery(id+"F0.imprint","IMPRINT",EDGE,{"disambiguationData":[TD([[subQ2,-1.0]])],"derivedFrom":subQ1}),-1.0]])]});}
            var Q2;
            {var subQ0=sQuery(id+"F0.wireOp",EDGE,"E24.MirrorCS");var subQ1=sQuery(id+"F0.wireOp",EDGE,"E0");var subQ2=makeQuery(id+"F0.imprint","INTERSECT",VERTEX,{"derivedFrom":[subQ1,subQ0]});Q2=makeQuery(id+"F0.imprint","IMPRINT",FACE,{"disambiguationData":[TD([[makeQuery(id+"F0.imprint","IMPRINT",EDGE,{"disambiguationData":[TD([[subQ2,-1.0]])],"derivedFrom":subQ1}),-1.0]])]});}
            var Q3;
            {var subQ0=sQuery(id+"F0.wireOp",EDGE,"E27.MirrorCS");var subQ1=sQuery(id+"F0.wireOp",EDGE,"E0");var subQ2=makeQuery(id+"F0.imprint","INTERSECT",VERTEX,{"derivedFrom":[subQ1,subQ0]});Q3=makeQuery(id+"F0.imprint","IMPRINT",FACE,{"disambiguationData":[TD([[makeQuery(id+"F0.imprint","IMPRINT",EDGE,{"disambiguationData":[TD([[subQ2,-1.0]])],"derivedFrom":subQ1}),-1.0]])]});}
            var Q4;
            {var subQ0=sQuery(id+"F0.wireOp",EDGE,"E29.MirrorCS");var subQ1=sQuery(id+"F0.wireOp",EDGE,"E0");var subQ2=makeQuery(id+"F0.imprint","INTERSECT",VERTEX,{"derivedFrom":[subQ1,subQ0]});Q4=makeQuery(id+"F0.imprint","IMPRINT",FACE,{"disambiguationData":[TD([[makeQuery(id+"F0.imprint","IMPRINT",EDGE,{"disambiguationData":[TD([[subQ2,-1.0]])],"derivedFrom":subQ1}),-1.0]])]});}
            var Q5;
            {var subQ0=sQuery(id+"F0.wireOp",EDGE,"E31.MirrorCS");var subQ1=sQuery(id+"F0.wireOp",EDGE,"E0");var subQ2=makeQuery(id+"F0.imprint","INTERSECT",VERTEX,{"derivedFrom":[subQ1,subQ0]});Q5=makeQuery(id+"F0.imprint","IMPRINT",FACE,{"disambiguationData":[TD([[makeQuery(id+"F0.imprint","IMPRINT",EDGE,{"disambiguationData":[TD([[subQ2,-1.0]])],"derivedFrom":subQ1}),-1.0]])]});}
            var Q6;
            {var subQ0=sQuery(id+"F0.wireOp",EDGE,"E33.MirrorCS");var subQ1=sQuery(id+"F0.wireOp",EDGE,"E0");var subQ2=makeQuery(id+"F0.imprint","INTERSECT",VERTEX,{"derivedFrom":[subQ1,subQ0]});Q6=makeQuery(id+"F0.imprint","IMPRINT",FACE,{"disambiguationData":[TD([[makeQuery(id+"F0.imprint","IMPRINT",EDGE,{"disambiguationData":[TD([[subQ2,-1.0]])],"derivedFrom":subQ1}),-1.0]])]});}
            var Q7;
            {var subQ0=sQuery(id+"F0.wireOp",EDGE,"E35.MirrorCS");var subQ1=sQuery(id+"F0.wireOp",EDGE,"E0");var subQ2=makeQuery(id+"F0.imprint","INTERSECT",VERTEX,{"derivedFrom":[subQ1,subQ0]});Q7=makeQuery(id+"F0.imprint","IMPRINT",FACE,{"disambiguationData":[TD([[makeQuery(id+"F0.imprint","IMPRINT",EDGE,{"disambiguationData":[TD([[subQ2,-1.0]])],"derivedFrom":subQ1}),-1.0]])]});}
            var Q8;
            {var subQ0=sQuery(id+"F0.wireOp",EDGE,"E37.MirrorCS");var subQ1=sQuery(id+"F0.wireOp",EDGE,"E0");var subQ2=makeQuery(id+"F0.imprint","INTERSECT",VERTEX,{"derivedFrom":[subQ1,subQ0]});Q8=makeQuery(id+"F0.imprint","IMPRINT",FACE,{"disambiguationData":[TD([[makeQuery(id+"F0.imprint","IMPRINT",EDGE,{"disambiguationData":[TD([[subQ2,-1.0]])],"derivedFrom":subQ1}),-1.0]])]});}
            var Q9;
            {var subQ0=sQuery(id+"F0.wireOp",EDGE,"E39.MirrorCS");var subQ1=sQuery(id+"F0.wireOp",EDGE,"E0");var subQ2=makeQuery(id+"F0.imprint","INTERSECT",VERTEX,{"derivedFrom":[subQ1,subQ0]});Q9=makeQuery(id+"F0.imprint","IMPRINT",FACE,{"disambiguationData":[TD([[makeQuery(id+"F0.imprint","IMPRINT",EDGE,{"disambiguationData":[TD([[subQ2,-1.0]])],"derivedFrom":subQ1}),-1.0]])]});}
            var Q10;
            {var subQ0=sQuery(id+"F0.wireOp",EDGE,"E41.MirrorCS");var subQ1=sQuery(id+"F0.wireOp",EDGE,"E0");var subQ2=makeQuery(id+"F0.imprint","INTERSECT",VERTEX,{"derivedFrom":[subQ1,subQ0]});Q10=makeQuery(id+"F0.imprint","IMPRINT",FACE,{"disambiguationData":[TD([[makeQuery(id+"F0.imprint","IMPRINT",EDGE,{"disambiguationData":[TD([[subQ2,-1.0]])],"derivedFrom":subQ1}),-1.0]])]});}
            var Q11;
            {var subQ0=sQuery(id+"F0.wireOp",EDGE,"E43.MirrorCS");var subQ1=sQuery(id+"F0.wireOp",EDGE,"E0");var subQ2=makeQuery(id+"F0.imprint","INTERSECT",VERTEX,{"derivedFrom":[subQ1,subQ0]});Q11=makeQuery(id+"F0.imprint","IMPRINT",FACE,{"disambiguationData":[TD([[makeQuery(id+"F0.imprint","IMPRINT",EDGE,{"disambiguationData":[TD([[subQ2,-1.0]])],"derivedFrom":subQ1}),-1.0]])]});}
            var Q12;
            {var subQ0=sQuery(id+"F0.wireOp",EDGE,"E45.MirrorCS");var subQ1=sQuery(id+"F0.wireOp",EDGE,"E0");var subQ2=makeQuery(id+"F0.imprint","INTERSECT",VERTEX,{"derivedFrom":[subQ1,subQ0]});Q12=makeQuery(id+"F0.imprint","IMPRINT",FACE,{"disambiguationData":[TD([[makeQuery(id+"F0.imprint","IMPRINT",EDGE,{"disambiguationData":[TD([[subQ2,-1.0]])],"derivedFrom":subQ1}),-1.0]])]});}
            var Q13;
            {var subQ0=sQuery(id+"F0.wireOp",EDGE,"E47.MirrorCS");var subQ1=sQuery(id+"F0.wireOp",EDGE,"E0");var subQ2=makeQuery(id+"F0.imprint","INTERSECT",VERTEX,{"derivedFrom":[subQ1,subQ0]});Q13=makeQuery(id+"F0.imprint","IMPRINT",FACE,{"disambiguationData":[TD([[makeQuery(id+"F0.imprint","IMPRINT",EDGE,{"disambiguationData":[TD([[subQ2,-1.0]])],"derivedFrom":subQ1}),-1.0]])]});}
            var Q14;
            {var subQ0=sQuery(id+"F0.wireOp",EDGE,"E50.MirrorCS");var subQ1=sQuery(id+"F0.wireOp",EDGE,"E0");var subQ2=makeQuery(id+"F0.imprint","INTERSECT",VERTEX,{"derivedFrom":[subQ1,subQ0]});Q14=makeQuery(id+"F0.imprint","IMPRINT",FACE,{"disambiguationData":[TD([[makeQuery(id+"F0.imprint","IMPRINT",EDGE,{"disambiguationData":[TD([[subQ2,-1.0]])],"derivedFrom":subQ1}),-1.0]])]});}
            var Q15;
            {var subQ0=sQuery(id+"F0.wireOp",EDGE,"E52.MirrorCS");var subQ1=sQuery(id+"F0.wireOp",EDGE,"E0");var subQ2=makeQuery(id+"F0.imprint","INTERSECT",VERTEX,{"derivedFrom":[subQ1,subQ0]});Q15=makeQuery(id+"F0.imprint","IMPRINT",FACE,{"disambiguationData":[TD([[makeQuery(id+"F0.imprint","IMPRINT",EDGE,{"disambiguationData":[TD([[subQ2,-1.0]])],"derivedFrom":subQ1}),-1.0]])]});}
            var Q16;
            {var subQ0=sQuery(id+"F0.wireOp",EDGE,"E54.MirrorCS");var subQ1=sQuery(id+"F0.wireOp",EDGE,"E0");var subQ2=makeQuery(id+"F0.imprint","INTERSECT",VERTEX,{"derivedFrom":[subQ1,subQ0]});Q16=makeQuery(id+"F0.imprint","IMPRINT",FACE,{"disambiguationData":[TD([[makeQuery(id+"F0.imprint","IMPRINT",EDGE,{"disambiguationData":[TD([[subQ2,-1.0]])],"derivedFrom":subQ1}),-1.0]])]});}
            var Q17;
            {var subQ0=sQuery(id+"F0.wireOp",EDGE,"E56.MirrorCS");var subQ1=sQuery(id+"F0.wireOp",EDGE,"E0");var subQ2=makeQuery(id+"F0.imprint","INTERSECT",VERTEX,{"derivedFrom":[subQ1,subQ0]});Q17=makeQuery(id+"F0.imprint","IMPRINT",FACE,{"disambiguationData":[TD([[makeQuery(id+"F0.imprint","IMPRINT",EDGE,{"disambiguationData":[TD([[subQ2,-1.0]])],"derivedFrom":subQ1}),-1.0]])]});}
            var Q18;
            {var subQ0=sQuery(id+"F0.wireOp",EDGE,"E58.MirrorCS");var subQ1=sQuery(id+"F0.wireOp",EDGE,"E0");var subQ2=makeQuery(id+"F0.imprint","INTERSECT",VERTEX,{"derivedFrom":[subQ1,subQ0]});Q18=makeQuery(id+"F0.imprint","IMPRINT",FACE,{"disambiguationData":[TD([[makeQuery(id+"F0.imprint","IMPRINT",EDGE,{"disambiguationData":[TD([[subQ2,-1.0]])],"derivedFrom":subQ1}),-1.0]])]});}
            var Q19;
            {var subQ0=sQuery(id+"F0.wireOp",EDGE,"E16.MirrorCS");var subQ1=sQuery(id+"F0.wireOp",EDGE,"E0");var subQ2=makeQuery(id+"F0.imprint","INTERSECT",VERTEX,{"derivedFrom":[subQ1,subQ0]});Q19=makeQuery(id+"F0.imprint","IMPRINT",FACE,{"disambiguationData":[TD([[makeQuery(id+"F0.imprint","IMPRINT",EDGE,{"disambiguationData":[TD([[subQ2,-1.0]])],"derivedFrom":subQ1}),-1.0]])]});}
            var Q20;
            {var subQ0=sQuery(id+"F0.wireOp",EDGE,"E63.MirrorCS");var subQ1=sQuery(id+"F0.wireOp",EDGE,"E0");var subQ2=makeQuery(id+"F0.imprint","INTERSECT",VERTEX,{"derivedFrom":[subQ1,subQ0]});Q20=makeQuery(id+"F0.imprint","IMPRINT",FACE,{"disambiguationData":[TD([[makeQuery(id+"F0.imprint","IMPRINT",EDGE,{"disambiguationData":[TD([[subQ2,-1.0]])],"derivedFrom":subQ1}),-1.0]])]});}
            var Q21;
            {var subQ0=sQuery(id+"F0.wireOp",EDGE,"E81.MirrorCS");var subQ1=sQuery(id+"F0.wireOp",EDGE,"E0");var subQ2=makeQuery(id+"F0.imprint","INTERSECT",VERTEX,{"derivedFrom":[subQ1,subQ0]});Q21=makeQuery(id+"F0.imprint","IMPRINT",FACE,{"disambiguationData":[TD([[makeQuery(id+"F0.imprint","IMPRINT",EDGE,{"disambiguationData":[TD([[subQ2,-1.0]])],"derivedFrom":subQ1}),-1.0]])]});}
            var Q22;
            {var subQ1=sQuery(id+"F0.wireOp",EDGE,"E0");var subQ5=sQuery(id+"F0.wireOp",EDGE,"E3.MirrorCS");var subQ6=makeQuery(id+"F0.imprint","INTERSECT",VERTEX,{"derivedFrom":[subQ1,subQ5]});Q22=makeQuery(id+"F0.imprint","IMPRINT",FACE,{"disambiguationData":[TD([[makeQuery(id+"F0.imprint","IMPRINT",EDGE,{"disambiguationData":[TD([[subQ6,-1.0]])],"derivedFrom":subQ1}),-1.0]])]});}
            var Q23;
            {var subQ0=sQuery(id+"F0.wireOp",EDGE,"E11.MirrorCS");var subQ1=sQuery(id+"F0.wireOp",EDGE,"E0");var subQ2=makeQuery(id+"F0.imprint","INTERSECT",VERTEX,{"derivedFrom":[subQ1,subQ0]});Q23=makeQuery(id+"F0.imprint","IMPRINT",FACE,{"disambiguationData":[TD([[makeQuery(id+"F0.imprint","IMPRINT",EDGE,{"disambiguationData":[TD([[subQ2,-1.0]])],"derivedFrom":subQ1}),-1.0]])]});}
            var Q24;
            {var subQ0=sQuery(id+"F0.wireOp",EDGE,"E20.MirrorCS");var subQ1=sQuery(id+"F0.wireOp",EDGE,"E0");var subQ2=makeQuery(id+"F0.imprint","INTERSECT",VERTEX,{"derivedFrom":[subQ1,subQ0]});Q24=makeQuery(id+"F0.imprint","IMPRINT",FACE,{"disambiguationData":[TD([[makeQuery(id+"F0.imprint","IMPRINT",EDGE,{"disambiguationData":[TD([[subQ2,-1.0]])],"derivedFrom":subQ1}),-1.0]])]});}
            var Q25;
            {var subQ0=sQuery(id+"F0.wireOp",EDGE,"E3.MirrorCS");var subQ1=sQuery(id+"F0.wireOp",EDGE,"E0");var subQ2=makeQuery(id+"F0.imprint","INTERSECT",VERTEX,{"derivedFrom":[subQ1,subQ0]});Q25=makeQuery(id+"F0.imprint","IMPRINT",FACE,{"disambiguationData":[TD([[makeQuery(id+"F0.imprint","IMPRINT",EDGE,{"disambiguationData":[TD([[subQ2,1.0]])],"derivedFrom":subQ1}),-1.0]])]});}
            var Q26;
            {var subQ0=sQuery(id+"F0.wireOp",EDGE,"E61.MirrorCS");var subQ1=sQuery(id+"F0.wireOp",EDGE,"E0");var subQ2=makeQuery(id+"F0.imprint","INTERSECT",VERTEX,{"derivedFrom":[subQ1,subQ0]});Q26=makeQuery(id+"F0.imprint","IMPRINT",FACE,{"disambiguationData":[TD([[makeQuery(id+"F0.imprint","IMPRINT",EDGE,{"disambiguationData":[TD([[subQ2,-1.0]])],"derivedFrom":subQ1}),-1.0]])]});}
            var Q27;
            {var subQ0=sQuery(id+"F0.wireOp",EDGE,"E65.MirrorCS");var subQ1=sQuery(id+"F0.wireOp",EDGE,"E0");var subQ2=makeQuery(id+"F0.imprint","INTERSECT",VERTEX,{"derivedFrom":[subQ1,subQ0]});Q27=makeQuery(id+"F0.imprint","IMPRINT",FACE,{"disambiguationData":[TD([[makeQuery(id+"F0.imprint","IMPRINT",EDGE,{"disambiguationData":[TD([[subQ2,-1.0]])],"derivedFrom":subQ1}),-1.0]])]});}
            var Q28;
            {var subQ0=sQuery(id+"F0.wireOp",EDGE,"E67.MirrorCS");var subQ1=sQuery(id+"F0.wireOp",EDGE,"E0");var subQ2=makeQuery(id+"F0.imprint","INTERSECT",VERTEX,{"derivedFrom":[subQ1,subQ0]});Q28=makeQuery(id+"F0.imprint","IMPRINT",FACE,{"disambiguationData":[TD([[makeQuery(id+"F0.imprint","IMPRINT",EDGE,{"disambiguationData":[TD([[subQ2,-1.0]])],"derivedFrom":subQ1}),-1.0]])]});}
            var Q29;
            {var subQ0=sQuery(id+"F0.wireOp",EDGE,"E69.MirrorCS");var subQ1=sQuery(id+"F0.wireOp",EDGE,"E0");var subQ2=makeQuery(id+"F0.imprint","INTERSECT",VERTEX,{"derivedFrom":[subQ1,subQ0]});Q29=makeQuery(id+"F0.imprint","IMPRINT",FACE,{"disambiguationData":[TD([[makeQuery(id+"F0.imprint","IMPRINT",EDGE,{"disambiguationData":[TD([[subQ2,-1.0]])],"derivedFrom":subQ1}),-1.0]])]});}
            var Q30;
            {var subQ0=sQuery(id+"F0.wireOp",EDGE,"E71.MirrorCS");var subQ1=sQuery(id+"F0.wireOp",EDGE,"E0");var subQ2=makeQuery(id+"F0.imprint","INTERSECT",VERTEX,{"derivedFrom":[subQ1,subQ0]});Q30=makeQuery(id+"F0.imprint","IMPRINT",FACE,{"disambiguationData":[TD([[makeQuery(id+"F0.imprint","IMPRINT",EDGE,{"disambiguationData":[TD([[subQ2,-1.0]])],"derivedFrom":subQ1}),-1.0]])]});}
            var Q31;
            {var subQ0=sQuery(id+"F0.wireOp",EDGE,"E73.MirrorCS");var subQ1=sQuery(id+"F0.wireOp",EDGE,"E0");var subQ2=makeQuery(id+"F0.imprint","INTERSECT",VERTEX,{"derivedFrom":[subQ1,subQ0]});Q31=makeQuery(id+"F0.imprint","IMPRINT",FACE,{"disambiguationData":[TD([[makeQuery(id+"F0.imprint","IMPRINT",EDGE,{"disambiguationData":[TD([[subQ2,-1.0]])],"derivedFrom":subQ1}),-1.0]])]});}
            var Q32;
            {var subQ0=sQuery(id+"F0.wireOp",EDGE,"E75.MirrorCS");var subQ1=sQuery(id+"F0.wireOp",EDGE,"E0");var subQ2=makeQuery(id+"F0.imprint","INTERSECT",VERTEX,{"derivedFrom":[subQ1,subQ0]});Q32=makeQuery(id+"F0.imprint","IMPRINT",FACE,{"disambiguationData":[TD([[makeQuery(id+"F0.imprint","IMPRINT",EDGE,{"disambiguationData":[TD([[subQ2,-1.0]])],"derivedFrom":subQ1}),-1.0]])]});}
            var Q33;
            {var subQ0=sQuery(id+"F0.wireOp",EDGE,"E77.MirrorCS");var subQ1=sQuery(id+"F0.wireOp",EDGE,"E0");var subQ2=makeQuery(id+"F0.imprint","INTERSECT",VERTEX,{"derivedFrom":[subQ1,subQ0]});Q33=makeQuery(id+"F0.imprint","IMPRINT",FACE,{"disambiguationData":[TD([[makeQuery(id+"F0.imprint","IMPRINT",EDGE,{"disambiguationData":[TD([[subQ2,-1.0]])],"derivedFrom":subQ1}),-1.0]])]});}
            var Q34;
            {var subQ0=sQuery(id+"F0.wireOp",EDGE,"E79.MirrorCS");var subQ1=sQuery(id+"F0.wireOp",EDGE,"E0");var subQ2=makeQuery(id+"F0.imprint","INTERSECT",VERTEX,{"derivedFrom":[subQ1,subQ0]});Q34=makeQuery(id+"F0.imprint","IMPRINT",FACE,{"disambiguationData":[TD([[makeQuery(id+"F0.imprint","IMPRINT",EDGE,{"disambiguationData":[TD([[subQ2,-1.0]])],"derivedFrom":subQ1}),-1.0]])]});}
            var Q35;
            {var subQ0=sQuery(id+"F0.wireOp",EDGE,"E83.MirrorCS");var subQ1=sQuery(id+"F0.wireOp",EDGE,"E0");var subQ2=makeQuery(id+"F0.imprint","INTERSECT",VERTEX,{"derivedFrom":[subQ1,subQ0]});Q35=makeQuery(id+"F0.imprint","IMPRINT",FACE,{"disambiguationData":[TD([[makeQuery(id+"F0.imprint","IMPRINT",EDGE,{"disambiguationData":[TD([[subQ2,-1.0]])],"derivedFrom":subQ1}),-1.0]])]});}
            var Q36;
            {var subQ0=sQuery(id+"F0.wireOp",EDGE,"E14.MirrorCS");var subQ1=sQuery(id+"F0.wireOp",EDGE,"E0");var subQ2=makeQuery(id+"F0.imprint","INTERSECT",VERTEX,{"derivedFrom":[subQ1,subQ0]});Q36=makeQuery(id+"F0.imprint","IMPRINT",FACE,{"disambiguationData":[TD([[makeQuery(id+"F0.imprint","IMPRINT",EDGE,{"disambiguationData":[TD([[subQ2,-1.0]])],"derivedFrom":subQ1}),-1.0]])]});}
            var Q37;
            {var subQ0=sQuery(id+"F0.wireOp",EDGE,"E18.MirrorCS");var subQ1=sQuery(id+"F0.wireOp",EDGE,"E0");var subQ2=makeQuery(id+"F0.imprint","INTERSECT",VERTEX,{"derivedFrom":[subQ1,subQ0]});Q37=makeQuery(id+"F0.imprint","IMPRINT",FACE,{"disambiguationData":[TD([[makeQuery(id+"F0.imprint","IMPRINT",EDGE,{"disambiguationData":[TD([[subQ2,-1.0]])],"derivedFrom":subQ1}),-1.0]])]});}
            extrude(context, id + "F1", {"entities" : qUnion([Q0, Q1, Q2, Q3, Q4, Q5, Q6, Q7, Q8, Q9, Q10, Q11, Q12, Q13, Q14, Q15, Q16, Q17, Q18, Q19, Q20, Q21, Q22, Q23, Q24, Q25, Q26, Q27, Q28, Q29, Q30, Q31, Q32, Q33, Q34, Q35, Q36, Q37]), "endBound" : BoundingType.SYMMETRIC, "depth" : 25 * mm});
        }
        {
            var Q0;
            Q0=makeQuery(id+"F1.opExtrude","SWEPT_EDGE",EDGE,{"disambiguationData":[OSD([sQuery(id+"F0.wireOp",EDGE,"E0"),sQuery(id+"F0.wireOp",EDGE,"E85.MirrorCS")])]});
            var Q1;
            Q1=makeQuery(id+"F1.opExtrude","SWEPT_EDGE",EDGE,{"disambiguationData":[OSD([sQuery(id+"F0.wireOp",EDGE,"E1"),sQuery(id+"F0.wireOp",EDGE,"E85.MirrorCS")])]});
            var Q2;
            Q2=makeQuery(id+"F1.opExtrude","SWEPT_EDGE",EDGE,{"disambiguationData":[OSD([sQuery(id+"F0.wireOp",EDGE,"E1"),sQuery(id+"F0.wireOp",EDGE,"E10.MirrorCS")])]});
            var Q3;
            Q3=makeQuery(id+"F1.opExtrude","SWEPT_EDGE",EDGE,{"disambiguationData":[OSD([sQuery(id+"F0.wireOp",EDGE,"E0"),sQuery(id+"F0.wireOp",EDGE,"E11.MirrorCS")])]});
            var Q4;
            Q4=makeQuery(id+"F1.opExtrude","SWEPT_EDGE",EDGE,{"disambiguationData":[OSD([sQuery(id+"F0.wireOp",EDGE,"E1"),sQuery(id+"F0.wireOp",EDGE,"E11.MirrorCS")])]});
            var Q5;
            Q5=makeQuery(id+"F1.opExtrude","SWEPT_EDGE",EDGE,{"disambiguationData":[OSD([sQuery(id+"F0.wireOp",EDGE,"E0"),sQuery(id+"F0.wireOp",EDGE,"E10.MirrorCS")])]});
            var Q6;
            Q6=makeQuery(id+"F1.opExtrude","SWEPT_EDGE",EDGE,{"disambiguationData":[OSD([sQuery(id+"F0.wireOp",EDGE,"E1"),sQuery(id+"F0.wireOp",EDGE,"E12.MirrorCS")])]});
            var Q7;
            Q7=makeQuery(id+"F1.opExtrude","SWEPT_EDGE",EDGE,{"disambiguationData":[OSD([sQuery(id+"F0.wireOp",EDGE,"E0"),sQuery(id+"F0.wireOp",EDGE,"E12.MirrorCS")])]});
            var Q8;
            Q8=makeQuery(id+"F1.opExtrude","SWEPT_EDGE",EDGE,{"disambiguationData":[OSD([sQuery(id+"F0.wireOp",EDGE,"E0"),sQuery(id+"F0.wireOp",EDGE,"E84.MirrorCS")])]});
            var Q9;
            Q9=makeQuery(id+"F1.opExtrude","SWEPT_EDGE",EDGE,{"disambiguationData":[OSD([sQuery(id+"F0.wireOp",EDGE,"E1"),sQuery(id+"F0.wireOp",EDGE,"E84.MirrorCS")])]});
            var Q10;
            Q10=makeQuery(id+"F1.opExtrude","SWEPT_EDGE",EDGE,{"disambiguationData":[OSD([sQuery(id+"F0.wireOp",EDGE,"E0"),sQuery(id+"F0.wireOp",EDGE,"E14.MirrorCS")])]});
            var Q11;
            Q11=makeQuery(id+"F1.opExtrude","SWEPT_EDGE",EDGE,{"disambiguationData":[OSD([sQuery(id+"F0.wireOp",EDGE,"E1"),sQuery(id+"F0.wireOp",EDGE,"E83.MirrorCS")])]});
            var Q12;
            Q12=makeQuery(id+"F1.opExtrude","SWEPT_EDGE",EDGE,{"disambiguationData":[OSD([sQuery(id+"F0.wireOp",EDGE,"E0"),sQuery(id+"F0.wireOp",EDGE,"E83.MirrorCS")])]});
            var Q13;
            Q13=makeQuery(id+"F1.opExtrude","CAP_EDGE",EDGE,{"disambiguationData":[OSD([sQuery(id+"F0.wireOp",EDGE,"E82.MirrorCS")])],"isStart":false});
            var Q14;
            Q14=makeQuery(id+"F1.opExtrude","SWEPT_EDGE",EDGE,{"disambiguationData":[OSD([sQuery(id+"F0.wireOp",EDGE,"E1"),sQuery(id+"F0.wireOp",EDGE,"E82.MirrorCS")])]});
            var Q15;
            Q15=makeQuery(id+"F1.opExtrude","SWEPT_EDGE",EDGE,{"disambiguationData":[OSD([sQuery(id+"F0.wireOp",EDGE,"E1"),sQuery(id+"F0.wireOp",EDGE,"E81.MirrorCS")])]});
            var Q16;
            Q16=makeQuery(id+"F1.opExtrude","SWEPT_EDGE",EDGE,{"disambiguationData":[OSD([sQuery(id+"F0.wireOp",EDGE,"E0"),sQuery(id+"F0.wireOp",EDGE,"E81.MirrorCS")])]});
            var Q17;
            Q17=makeQuery(id+"F1.opExtrude","SWEPT_EDGE",EDGE,{"disambiguationData":[OSD([sQuery(id+"F0.wireOp",EDGE,"E0"),sQuery(id+"F0.wireOp",EDGE,"E80.MirrorCS")])]});
            var Q18;
            Q18=makeQuery(id+"F1.opExtrude","SWEPT_EDGE",EDGE,{"disambiguationData":[OSD([sQuery(id+"F0.wireOp",EDGE,"E1"),sQuery(id+"F0.wireOp",EDGE,"E80.MirrorCS")])]});
            var Q19;
            Q19=makeQuery(id+"F1.opExtrude","SWEPT_EDGE",EDGE,{"disambiguationData":[OSD([sQuery(id+"F0.wireOp",EDGE,"E1"),sQuery(id+"F0.wireOp",EDGE,"E79.MirrorCS")])]});
            var Q20;
            Q20=makeQuery(id+"F1.opExtrude","CAP_EDGE",EDGE,{"disambiguationData":[OSD([sQuery(id+"F0.wireOp",EDGE,"E79.MirrorCS")])],"isStart":false});
            var Q21;
            Q21=makeQuery(id+"F1.opExtrude","SWEPT_EDGE",EDGE,{"disambiguationData":[OSD([sQuery(id+"F0.wireOp",EDGE,"E0"),sQuery(id+"F0.wireOp",EDGE,"E78.MirrorCS")])]});
            var Q22;
            Q22=makeQuery(id+"F1.opExtrude","SWEPT_EDGE",EDGE,{"disambiguationData":[OSD([sQuery(id+"F0.wireOp",EDGE,"E1"),sQuery(id+"F0.wireOp",EDGE,"E78.MirrorCS")])]});
            var Q23;
            Q23=makeQuery(id+"F1.opExtrude","SWEPT_EDGE",EDGE,{"disambiguationData":[OSD([sQuery(id+"F0.wireOp",EDGE,"E1"),sQuery(id+"F0.wireOp",EDGE,"E77.MirrorCS")])]});
            var Q24;
            Q24=makeQuery(id+"F1.opExtrude","CAP_EDGE",EDGE,{"disambiguationData":[OSD([sQuery(id+"F0.wireOp",EDGE,"E77.MirrorCS")])],"isStart":false});
            var Q25;
            Q25=makeQuery(id+"F1.opExtrude","SWEPT_EDGE",EDGE,{"disambiguationData":[OSD([sQuery(id+"F0.wireOp",EDGE,"E0"),sQuery(id+"F0.wireOp",EDGE,"E76.MirrorCS")])]});
            var Q26;
            Q26=makeQuery(id+"F1.opExtrude","SWEPT_EDGE",EDGE,{"disambiguationData":[OSD([sQuery(id+"F0.wireOp",EDGE,"E1"),sQuery(id+"F0.wireOp",EDGE,"E76.MirrorCS")])]});
            var Q27;
            Q27=makeQuery(id+"F1.opExtrude","SWEPT_EDGE",EDGE,{"disambiguationData":[OSD([sQuery(id+"F0.wireOp",EDGE,"E1"),sQuery(id+"F0.wireOp",EDGE,"E75.MirrorCS")])]});
            var Q28;
            Q28=makeQuery(id+"F1.opExtrude","SWEPT_EDGE",EDGE,{"disambiguationData":[OSD([sQuery(id+"F0.wireOp",EDGE,"E0"),sQuery(id+"F0.wireOp",EDGE,"E75.MirrorCS")])]});
            var Q29;
            Q29=makeQuery(id+"F1.opExtrude","SWEPT_EDGE",EDGE,{"disambiguationData":[OSD([sQuery(id+"F0.wireOp",EDGE,"E0"),sQuery(id+"F0.wireOp",EDGE,"E74.MirrorCS")])]});
            var Q30;
            Q30=makeQuery(id+"F1.opExtrude","SWEPT_EDGE",EDGE,{"disambiguationData":[OSD([sQuery(id+"F0.wireOp",EDGE,"E1"),sQuery(id+"F0.wireOp",EDGE,"E74.MirrorCS")])]});
            var Q31;
            Q31=makeQuery(id+"F1.opExtrude","SWEPT_EDGE",EDGE,{"disambiguationData":[OSD([sQuery(id+"F0.wireOp",EDGE,"E1"),sQuery(id+"F0.wireOp",EDGE,"E73.MirrorCS")])]});
            var Q32;
            Q32=makeQuery(id+"F1.opExtrude","SWEPT_EDGE",EDGE,{"disambiguationData":[OSD([sQuery(id+"F0.wireOp",EDGE,"E0"),sQuery(id+"F0.wireOp",EDGE,"E73.MirrorCS")])]});
            var Q33;
            Q33=makeQuery(id+"F1.opExtrude","SWEPT_EDGE",EDGE,{"disambiguationData":[OSD([sQuery(id+"F0.wireOp",EDGE,"E1"),sQuery(id+"F0.wireOp",EDGE,"E14.MirrorCS")])]});
            var Q34;
            Q34=makeQuery(id+"F1.opExtrude","SWEPT_EDGE",EDGE,{"disambiguationData":[OSD([sQuery(id+"F0.wireOp",EDGE,"E1"),sQuery(id+"F0.wireOp",EDGE,"E15.MirrorCS")])]});
            var Q35;
            Q35=makeQuery(id+"F1.opExtrude","SWEPT_EDGE",EDGE,{"disambiguationData":[OSD([sQuery(id+"F0.wireOp",EDGE,"E1"),sQuery(id+"F0.wireOp",EDGE,"E16.MirrorCS")])]});
            var Q36;
            Q36=makeQuery(id+"F1.opExtrude","SWEPT_EDGE",EDGE,{"disambiguationData":[OSD([sQuery(id+"F0.wireOp",EDGE,"E0"),sQuery(id+"F0.wireOp",EDGE,"E16.MirrorCS")])]});
            var Q37;
            Q37=makeQuery(id+"F1.opExtrude","SWEPT_EDGE",EDGE,{"disambiguationData":[OSD([sQuery(id+"F0.wireOp",EDGE,"E1"),sQuery(id+"F0.wireOp",EDGE,"E17.MirrorCS")])]});
            var Q38;
            Q38=makeQuery(id+"F1.opExtrude","SWEPT_EDGE",EDGE,{"disambiguationData":[OSD([sQuery(id+"F0.wireOp",EDGE,"E0"),sQuery(id+"F0.wireOp",EDGE,"E18.MirrorCS")])]});
            var Q39;
            Q39=makeQuery(id+"F1.opExtrude","SWEPT_EDGE",EDGE,{"disambiguationData":[OSD([sQuery(id+"F0.wireOp",EDGE,"E1"),sQuery(id+"F0.wireOp",EDGE,"E18.MirrorCS")])]});
            var Q40;
            Q40=makeQuery(id+"F1.opExtrude","SWEPT_EDGE",EDGE,{"disambiguationData":[OSD([sQuery(id+"F0.wireOp",EDGE,"E1"),sQuery(id+"F0.wireOp",EDGE,"E19.MirrorCS")])]});
            var Q41;
            Q41=makeQuery(id+"F1.opExtrude","SWEPT_EDGE",EDGE,{"disambiguationData":[OSD([sQuery(id+"F0.wireOp",EDGE,"E0"),sQuery(id+"F0.wireOp",EDGE,"E15.MirrorCS")])]});
            var Q42;
            Q42=makeQuery(id+"F1.opExtrude","SWEPT_EDGE",EDGE,{"disambiguationData":[OSD([sQuery(id+"F0.wireOp",EDGE,"E0"),sQuery(id+"F0.wireOp",EDGE,"E17.MirrorCS")])]});
            var Q43;
            Q43=makeQuery(id+"F1.opExtrude","SWEPT_EDGE",EDGE,{"disambiguationData":[OSD([sQuery(id+"F0.wireOp",EDGE,"E0"),sQuery(id+"F0.wireOp",EDGE,"E19.MirrorCS")])]});
            var Q44;
            Q44=makeQuery(id+"F1.opExtrude","SWEPT_EDGE",EDGE,{"disambiguationData":[OSD([sQuery(id+"F0.wireOp",EDGE,"E1"),sQuery(id+"F0.wireOp",EDGE,"E20.MirrorCS")])]});
            var Q45;
            Q45=makeQuery(id+"F1.opExtrude","SWEPT_EDGE",EDGE,{"disambiguationData":[OSD([sQuery(id+"F0.wireOp",EDGE,"E1"),sQuery(id+"F0.wireOp",EDGE,"E21.MirrorCS")])]});
            var Q46;
            Q46=makeQuery(id+"F1.opExtrude","SWEPT_FACE",FACE,{"disambiguationData":[OSD([sQuery(id+"F0.wireOp",EDGE,"E21.MirrorCS")])]});
            var Q47;
            Q47=makeQuery(id+"F1.opExtrude","SWEPT_EDGE",EDGE,{"disambiguationData":[OSD([sQuery(id+"F0.wireOp",EDGE,"E1"),sQuery(id+"F0.wireOp",EDGE,"E22.MirrorCS")])]});
            var Q48;
            {var subQ0=sQuery(id+"F0.wireOp",EDGE,"E1");Q48=makeQuery(id+"F1.opExtrude","SWEPT_FACE",FACE,{"disambiguationData":[OSD([subQ0]),TDD([makeQuery(id+"F0.imprint","IMPRINT",EDGE,{"disambiguationData":[TD([[makeQuery(id+"F0.imprint","INTERSECT",VERTEX,{"derivedFrom":[subQ0,sQuery(id+"F0.wireOp",EDGE,"E22.MirrorCS")]}),-1.0]])],"derivedFrom":subQ0})])]});}
            var Q49;
            Q49=makeQuery(id+"F1.opExtrude","SWEPT_EDGE",EDGE,{"disambiguationData":[OSD([sQuery(id+"F0.wireOp",EDGE,"E0"),sQuery(id+"F0.wireOp",EDGE,"E23.MirrorCS")])]});
            var Q50;
            Q50=makeQuery(id+"F1.opExtrude","SWEPT_EDGE",EDGE,{"disambiguationData":[OSD([sQuery(id+"F0.wireOp",EDGE,"E0"),sQuery(id+"F0.wireOp",EDGE,"E24.MirrorCS")])]});
            var Q51;
            Q51=makeQuery(id+"F1.opExtrude","SWEPT_EDGE",EDGE,{"disambiguationData":[OSD([sQuery(id+"F0.wireOp",EDGE,"E1"),sQuery(id+"F0.wireOp",EDGE,"E24.MirrorCS")])]});
            var Q52;
            Q52=makeQuery(id+"F1.opExtrude","SWEPT_EDGE",EDGE,{"disambiguationData":[OSD([sQuery(id+"F0.wireOp",EDGE,"E1"),sQuery(id+"F0.wireOp",EDGE,"E25.MirrorCS")])]});
            var Q53;
            Q53=makeQuery(id+"F1.opExtrude","SWEPT_EDGE",EDGE,{"disambiguationData":[OSD([sQuery(id+"F0.wireOp",EDGE,"E0"),sQuery(id+"F0.wireOp",EDGE,"E20.MirrorCS")])]});
            var Q54;
            Q54=makeQuery(id+"F1.opExtrude","SWEPT_EDGE",EDGE,{"disambiguationData":[OSD([sQuery(id+"F0.wireOp",EDGE,"E0"),sQuery(id+"F0.wireOp",EDGE,"E22.MirrorCS")])]});
            var Q55;
            Q55=makeQuery(id+"F1.opExtrude","SWEPT_EDGE",EDGE,{"disambiguationData":[OSD([sQuery(id+"F0.wireOp",EDGE,"E0"),sQuery(id+"F0.wireOp",EDGE,"E25.MirrorCS")])]});
            var Q56;
            Q56=makeQuery(id+"F1.opExtrude","SWEPT_EDGE",EDGE,{"disambiguationData":[OSD([sQuery(id+"F0.wireOp",EDGE,"E0"),sQuery(id+"F0.wireOp",EDGE,"E28.MirrorCS")])]});
            var Q57;
            Q57=makeQuery(id+"F1.opExtrude","SWEPT_EDGE",EDGE,{"disambiguationData":[OSD([sQuery(id+"F0.wireOp",EDGE,"E1"),sQuery(id+"F0.wireOp",EDGE,"E28.MirrorCS")])]});
            var Q58;
            Q58=makeQuery(id+"F1.opExtrude","SWEPT_EDGE",EDGE,{"disambiguationData":[OSD([sQuery(id+"F0.wireOp",EDGE,"E1"),sQuery(id+"F0.wireOp",EDGE,"E27.MirrorCS")])]});
            var Q59;
            Q59=makeQuery(id+"F1.opExtrude","SWEPT_EDGE",EDGE,{"disambiguationData":[OSD([sQuery(id+"F0.wireOp",EDGE,"E0"),sQuery(id+"F0.wireOp",EDGE,"E27.MirrorCS")])]});
            var Q60;
            Q60=makeQuery(id+"F1.opExtrude","SWEPT_EDGE",EDGE,{"disambiguationData":[OSD([sQuery(id+"F0.wireOp",EDGE,"E0"),sQuery(id+"F0.wireOp",EDGE,"E29.MirrorCS")])]});
            var Q61;
            Q61=makeQuery(id+"F1.opExtrude","SWEPT_EDGE",EDGE,{"disambiguationData":[OSD([sQuery(id+"F0.wireOp",EDGE,"E1"),sQuery(id+"F0.wireOp",EDGE,"E29.MirrorCS")])]});
            var Q62;
            Q62=makeQuery(id+"F1.opExtrude","SWEPT_EDGE",EDGE,{"disambiguationData":[OSD([sQuery(id+"F0.wireOp",EDGE,"E1"),sQuery(id+"F0.wireOp",EDGE,"E30.MirrorCS")])]});
            var Q63;
            Q63=makeQuery(id+"F1.opExtrude","SWEPT_EDGE",EDGE,{"disambiguationData":[OSD([sQuery(id+"F0.wireOp",EDGE,"E0"),sQuery(id+"F0.wireOp",EDGE,"E31.MirrorCS")])]});
            var Q64;
            Q64=makeQuery(id+"F1.opExtrude","SWEPT_EDGE",EDGE,{"disambiguationData":[OSD([sQuery(id+"F0.wireOp",EDGE,"E1"),sQuery(id+"F0.wireOp",EDGE,"E31.MirrorCS")])]});
            var Q65;
            Q65=makeQuery(id+"F1.opExtrude","SWEPT_EDGE",EDGE,{"disambiguationData":[OSD([sQuery(id+"F0.wireOp",EDGE,"E1"),sQuery(id+"F0.wireOp",EDGE,"E32.MirrorCS")])]});
            var Q66;
            Q66=makeQuery(id+"F1.opExtrude","SWEPT_EDGE",EDGE,{"disambiguationData":[OSD([sQuery(id+"F0.wireOp",EDGE,"E0"),sQuery(id+"F0.wireOp",EDGE,"E30.MirrorCS")])]});
            var Q67;
            Q67=makeQuery(id+"F1.opExtrude","SWEPT_EDGE",EDGE,{"disambiguationData":[OSD([sQuery(id+"F0.wireOp",EDGE,"E0"),sQuery(id+"F0.wireOp",EDGE,"E32.MirrorCS")])]});
            var Q68;
            Q68=makeQuery(id+"F1.opExtrude","SWEPT_EDGE",EDGE,{"disambiguationData":[OSD([sQuery(id+"F0.wireOp",EDGE,"E0"),sQuery(id+"F0.wireOp",EDGE,"E34.MirrorCS")])]});
            var Q69;
            Q69=makeQuery(id+"F1.opExtrude","SWEPT_EDGE",EDGE,{"disambiguationData":[OSD([sQuery(id+"F0.wireOp",EDGE,"E0"),sQuery(id+"F0.wireOp",EDGE,"E36.MirrorCS")])]});
            var Q70;
            Q70=makeQuery(id+"F1.opExtrude","SWEPT_EDGE",EDGE,{"disambiguationData":[OSD([sQuery(id+"F0.wireOp",EDGE,"E1"),sQuery(id+"F0.wireOp",EDGE,"E36.MirrorCS")])]});
            var Q71;
            Q71=makeQuery(id+"F1.opExtrude","SWEPT_EDGE",EDGE,{"disambiguationData":[OSD([sQuery(id+"F0.wireOp",EDGE,"E1"),sQuery(id+"F0.wireOp",EDGE,"E35.MirrorCS")])]});
            var Q72;
            Q72=makeQuery(id+"F1.opExtrude","SWEPT_EDGE",EDGE,{"disambiguationData":[OSD([sQuery(id+"F0.wireOp",EDGE,"E1"),sQuery(id+"F0.wireOp",EDGE,"E34.MirrorCS")])]});
            var Q73;
            Q73=makeQuery(id+"F1.opExtrude","SWEPT_EDGE",EDGE,{"disambiguationData":[OSD([sQuery(id+"F0.wireOp",EDGE,"E1"),sQuery(id+"F0.wireOp",EDGE,"E33.MirrorCS")])]});
            var Q74;
            Q74=makeQuery(id+"F1.opExtrude","SWEPT_EDGE",EDGE,{"disambiguationData":[OSD([sQuery(id+"F0.wireOp",EDGE,"E0"),sQuery(id+"F0.wireOp",EDGE,"E33.MirrorCS")])]});
            var Q75;
            Q75=makeQuery(id+"F1.opExtrude","SWEPT_EDGE",EDGE,{"disambiguationData":[OSD([sQuery(id+"F0.wireOp",EDGE,"E0"),sQuery(id+"F0.wireOp",EDGE,"E35.MirrorCS")])]});
            var Q76;
            Q76=makeQuery(id+"F1.opExtrude","SWEPT_EDGE",EDGE,{"disambiguationData":[OSD([sQuery(id+"F0.wireOp",EDGE,"E0"),sQuery(id+"F0.wireOp",EDGE,"E37.MirrorCS")])]});
            var Q77;
            Q77=makeQuery(id+"F1.opExtrude","SWEPT_EDGE",EDGE,{"disambiguationData":[OSD([sQuery(id+"F0.wireOp",EDGE,"E1"),sQuery(id+"F0.wireOp",EDGE,"E37.MirrorCS")])]});
            var Q78;
            {var subQ0=sQuery(id+"F0.wireOp",EDGE,"E1");Q78=makeQuery(id+"F1.opExtrude","SWEPT_FACE",FACE,{"disambiguationData":[OSD([subQ0]),TDD([makeQuery(id+"F0.imprint","IMPRINT",EDGE,{"disambiguationData":[TD([[makeQuery(id+"F0.imprint","INTERSECT",VERTEX,{"derivedFrom":[subQ0,sQuery(id+"F0.wireOp",EDGE,"E37.MirrorCS")]}),-1.0]])],"derivedFrom":subQ0})])]});}
            var Q79;
            Q79=makeQuery(id+"F1.opExtrude","SWEPT_EDGE",EDGE,{"disambiguationData":[OSD([sQuery(id+"F0.wireOp",EDGE,"E0"),sQuery(id+"F0.wireOp",EDGE,"E38.MirrorCS")])]});
            var Q80;
            Q80=makeQuery(id+"F1.opExtrude","SWEPT_EDGE",EDGE,{"disambiguationData":[OSD([sQuery(id+"F0.wireOp",EDGE,"E1"),sQuery(id+"F0.wireOp",EDGE,"E39.MirrorCS")])]});
            var Q81;
            {var subQ0=sQuery(id+"F0.wireOp",EDGE,"E1");Q81=makeQuery(id+"F1.opExtrude","SWEPT_FACE",FACE,{"disambiguationData":[OSD([subQ0]),TDD([makeQuery(id+"F0.imprint","IMPRINT",EDGE,{"disambiguationData":[TD([[makeQuery(id+"F0.imprint","INTERSECT",VERTEX,{"derivedFrom":[subQ0,sQuery(id+"F0.wireOp",EDGE,"E39.MirrorCS")]}),-1.0]])],"derivedFrom":subQ0})])]});}
            var Q82;
            Q82=makeQuery(id+"F1.opExtrude","SWEPT_EDGE",EDGE,{"disambiguationData":[OSD([sQuery(id+"F0.wireOp",EDGE,"E0"),sQuery(id+"F0.wireOp",EDGE,"E39.MirrorCS")])]});
            var Q83;
            Q83=makeQuery(id+"F1.opExtrude","SWEPT_EDGE",EDGE,{"disambiguationData":[OSD([sQuery(id+"F0.wireOp",EDGE,"E0"),sQuery(id+"F0.wireOp",EDGE,"E40.MirrorCS")])]});
            var Q84;
            Q84=makeQuery(id+"F1.opExtrude","SWEPT_EDGE",EDGE,{"disambiguationData":[OSD([sQuery(id+"F0.wireOp",EDGE,"E0"),sQuery(id+"F0.wireOp",EDGE,"E41.MirrorCS")])]});
            var Q85;
            Q85=makeQuery(id+"F1.opExtrude","SWEPT_EDGE",EDGE,{"disambiguationData":[OSD([sQuery(id+"F0.wireOp",EDGE,"E1"),sQuery(id+"F0.wireOp",EDGE,"E41.MirrorCS")])]});
            var Q86;
            Q86=makeQuery(id+"F1.opExtrude","SWEPT_EDGE",EDGE,{"disambiguationData":[OSD([sQuery(id+"F0.wireOp",EDGE,"E1"),sQuery(id+"F0.wireOp",EDGE,"E42.MirrorCS")])]});
            var Q87;
            Q87=makeQuery(id+"F1.opExtrude","SWEPT_EDGE",EDGE,{"disambiguationData":[OSD([sQuery(id+"F0.wireOp",EDGE,"E0"),sQuery(id+"F0.wireOp",EDGE,"E43.MirrorCS")])]});
            var Q88;
            Q88=makeQuery(id+"F1.opExtrude","SWEPT_EDGE",EDGE,{"disambiguationData":[OSD([sQuery(id+"F0.wireOp",EDGE,"E1"),sQuery(id+"F0.wireOp",EDGE,"E43.MirrorCS")])]});
            var Q89;
            Q89=makeQuery(id+"F1.opExtrude","SWEPT_EDGE",EDGE,{"disambiguationData":[OSD([sQuery(id+"F0.wireOp",EDGE,"E1"),sQuery(id+"F0.wireOp",EDGE,"E44.MirrorCS")])]});
            var Q90;
            Q90=makeQuery(id+"F1.opExtrude","SWEPT_EDGE",EDGE,{"disambiguationData":[OSD([sQuery(id+"F0.wireOp",EDGE,"E0"),sQuery(id+"F0.wireOp",EDGE,"E42.MirrorCS")])]});
            var Q91;
            Q91=makeQuery(id+"F1.opExtrude","SWEPT_EDGE",EDGE,{"disambiguationData":[OSD([sQuery(id+"F0.wireOp",EDGE,"E0"),sQuery(id+"F0.wireOp",EDGE,"E44.MirrorCS")])]});
            var Q92;
            Q92=makeQuery(id+"F1.opExtrude","SWEPT_EDGE",EDGE,{"disambiguationData":[OSD([sQuery(id+"F0.wireOp",EDGE,"E1"),sQuery(id+"F0.wireOp",EDGE,"E45.MirrorCS")])]});
            var Q93;
            {var subQ0=sQuery(id+"F0.wireOp",EDGE,"E1");Q93=makeQuery(id+"F1.opExtrude","SWEPT_FACE",FACE,{"disambiguationData":[OSD([subQ0]),TDD([makeQuery(id+"F0.imprint","IMPRINT",EDGE,{"disambiguationData":[TD([[makeQuery(id+"F0.imprint","INTERSECT",VERTEX,{"derivedFrom":[subQ0,sQuery(id+"F0.wireOp",EDGE,"E45.MirrorCS")]}),-1.0]])],"derivedFrom":subQ0})])]});}
            var Q94;
            Q94=makeQuery(id+"F1.opExtrude","SWEPT_EDGE",EDGE,{"disambiguationData":[OSD([sQuery(id+"F0.wireOp",EDGE,"E0"),sQuery(id+"F0.wireOp",EDGE,"E46.MirrorCS")])]});
            var Q95;
            Q95=makeQuery(id+"F1.opExtrude","SWEPT_EDGE",EDGE,{"disambiguationData":[OSD([sQuery(id+"F0.wireOp",EDGE,"E0"),sQuery(id+"F0.wireOp",EDGE,"E45.MirrorCS")])]});
            var Q96;
            Q96=makeQuery(id+"F1.opExtrude","SWEPT_EDGE",EDGE,{"disambiguationData":[OSD([sQuery(id+"F0.wireOp",EDGE,"E0"),sQuery(id+"F0.wireOp",EDGE,"E47.MirrorCS")])]});
            var Q97;
            Q97=makeQuery(id+"F1.opExtrude","SWEPT_EDGE",EDGE,{"disambiguationData":[OSD([sQuery(id+"F0.wireOp",EDGE,"E1"),sQuery(id+"F0.wireOp",EDGE,"E47.MirrorCS")])]});
            var Q98;
            Q98=makeQuery(id+"F1.opExtrude","SWEPT_EDGE",EDGE,{"disambiguationData":[OSD([sQuery(id+"F0.wireOp",EDGE,"E1"),sQuery(id+"F0.wireOp",EDGE,"E49.MirrorCS")])]});
            var Q99;
            Q99=makeQuery(id+"F1.opExtrude","SWEPT_EDGE",EDGE,{"disambiguationData":[OSD([sQuery(id+"F0.wireOp",EDGE,"E0"),sQuery(id+"F0.wireOp",EDGE,"E50.MirrorCS")])]});
            var Q100;
            Q100=makeQuery(id+"F1.opExtrude","SWEPT_EDGE",EDGE,{"disambiguationData":[OSD([sQuery(id+"F0.wireOp",EDGE,"E1"),sQuery(id+"F0.wireOp",EDGE,"E50.MirrorCS")])]});
            var Q101;
            Q101=makeQuery(id+"F1.opExtrude","SWEPT_EDGE",EDGE,{"disambiguationData":[OSD([sQuery(id+"F0.wireOp",EDGE,"E1"),sQuery(id+"F0.wireOp",EDGE,"E51.MirrorCS")])]});
            var Q102;
            Q102=makeQuery(id+"F1.opExtrude","SWEPT_EDGE",EDGE,{"disambiguationData":[OSD([sQuery(id+"F0.wireOp",EDGE,"E0"),sQuery(id+"F0.wireOp",EDGE,"E49.MirrorCS")])]});
            var Q103;
            Q103=makeQuery(id+"F1.opExtrude","SWEPT_EDGE",EDGE,{"disambiguationData":[OSD([sQuery(id+"F0.wireOp",EDGE,"E0"),sQuery(id+"F0.wireOp",EDGE,"E51.MirrorCS")])]});
            var Q104;
            Q104=makeQuery(id+"F1.opExtrude","SWEPT_EDGE",EDGE,{"disambiguationData":[OSD([sQuery(id+"F0.wireOp",EDGE,"E0"),sQuery(id+"F0.wireOp",EDGE,"E52.MirrorCS")])]});
            var Q105;
            Q105=makeQuery(id+"F1.opExtrude","SWEPT_EDGE",EDGE,{"disambiguationData":[OSD([sQuery(id+"F0.wireOp",EDGE,"E1"),sQuery(id+"F0.wireOp",EDGE,"E52.MirrorCS")])]});
            var Q106;
            Q106=makeQuery(id+"F1.opExtrude","SWEPT_EDGE",EDGE,{"disambiguationData":[OSD([sQuery(id+"F0.wireOp",EDGE,"E1"),sQuery(id+"F0.wireOp",EDGE,"E53.MirrorCS")])]});
            var Q107;
            Q107=makeQuery(id+"F1.opExtrude","SWEPT_EDGE",EDGE,{"disambiguationData":[OSD([sQuery(id+"F0.wireOp",EDGE,"E0"),sQuery(id+"F0.wireOp",EDGE,"E54.MirrorCS")])]});
            var Q108;
            Q108=makeQuery(id+"F1.opExtrude","SWEPT_EDGE",EDGE,{"disambiguationData":[OSD([sQuery(id+"F0.wireOp",EDGE,"E1"),sQuery(id+"F0.wireOp",EDGE,"E54.MirrorCS")])]});
            var Q109;
            Q109=makeQuery(id+"F1.opExtrude","SWEPT_EDGE",EDGE,{"disambiguationData":[OSD([sQuery(id+"F0.wireOp",EDGE,"E1"),sQuery(id+"F0.wireOp",EDGE,"E55.MirrorCS")])]});
            var Q110;
            Q110=makeQuery(id+"F1.opExtrude","SWEPT_EDGE",EDGE,{"disambiguationData":[OSD([sQuery(id+"F0.wireOp",EDGE,"E0"),sQuery(id+"F0.wireOp",EDGE,"E53.MirrorCS")])]});
            var Q111;
            Q111=makeQuery(id+"F1.opExtrude","SWEPT_EDGE",EDGE,{"disambiguationData":[OSD([sQuery(id+"F0.wireOp",EDGE,"E0"),sQuery(id+"F0.wireOp",EDGE,"E56.MirrorCS")])]});
            var Q112;
            Q112=makeQuery(id+"F1.opExtrude","SWEPT_EDGE",EDGE,{"disambiguationData":[OSD([sQuery(id+"F0.wireOp",EDGE,"E1"),sQuery(id+"F0.wireOp",EDGE,"E56.MirrorCS")])]});
            var Q113;
            Q113=makeQuery(id+"F1.opExtrude","SWEPT_EDGE",EDGE,{"disambiguationData":[OSD([sQuery(id+"F0.wireOp",EDGE,"E0"),sQuery(id+"F0.wireOp",EDGE,"E58.MirrorCS")])]});
            var Q114;
            Q114=makeQuery(id+"F1.opExtrude","SWEPT_EDGE",EDGE,{"disambiguationData":[OSD([sQuery(id+"F0.wireOp",EDGE,"E1"),sQuery(id+"F0.wireOp",EDGE,"E58.MirrorCS")])]});
            var Q115;
            Q115=makeQuery(id+"F1.opExtrude","SWEPT_EDGE",EDGE,{"disambiguationData":[OSD([sQuery(id+"F0.wireOp",EDGE,"E1"),sQuery(id+"F0.wireOp",EDGE,"E59.MirrorCS")])]});
            var Q116;
            Q116=makeQuery(id+"F1.opExtrude","SWEPT_EDGE",EDGE,{"disambiguationData":[OSD([sQuery(id+"F0.wireOp",EDGE,"E1"),sQuery(id+"F0.wireOp",EDGE,"E57.MirrorCS")])]});
            var Q117;
            Q117=makeQuery(id+"F1.opExtrude","SWEPT_EDGE",EDGE,{"disambiguationData":[OSD([sQuery(id+"F0.wireOp",EDGE,"E0"),sQuery(id+"F0.wireOp",EDGE,"E57.MirrorCS")])]});
            var Q118;
            Q118=makeQuery(id+"F1.opExtrude","SWEPT_EDGE",EDGE,{"disambiguationData":[OSD([sQuery(id+"F0.wireOp",EDGE,"E0"),sQuery(id+"F0.wireOp",EDGE,"E55.MirrorCS")])]});
            var Q119;
            Q119=makeQuery(id+"F1.opExtrude","SWEPT_EDGE",EDGE,{"disambiguationData":[OSD([sQuery(id+"F0.wireOp",EDGE,"E0"),sQuery(id+"F0.wireOp",EDGE,"E59.MirrorCS")])]});
            var Q120;
            Q120=makeQuery(id+"F1.opExtrude","SWEPT_EDGE",EDGE,{"disambiguationData":[OSD([sQuery(id+"F0.wireOp",EDGE,"E1"),sQuery(id+"F0.wireOp",EDGE,"E61.MirrorCS")])]});
            var Q121;
            Q121=makeQuery(id+"F1.opExtrude","SWEPT_EDGE",EDGE,{"disambiguationData":[OSD([sQuery(id+"F0.wireOp",EDGE,"E1"),sQuery(id+"F0.wireOp",EDGE,"E62.MirrorCS")])]});
            var Q122;
            Q122=makeQuery(id+"F1.opExtrude","SWEPT_EDGE",EDGE,{"disambiguationData":[OSD([sQuery(id+"F0.wireOp",EDGE,"E0"),sQuery(id+"F0.wireOp",EDGE,"E62.MirrorCS")])]});
            var Q123;
            Q123=makeQuery(id+"F1.opExtrude","SWEPT_EDGE",EDGE,{"disambiguationData":[OSD([sQuery(id+"F0.wireOp",EDGE,"E1"),sQuery(id+"F0.wireOp",EDGE,"E63.MirrorCS")])]});
            var Q124;
            Q124=makeQuery(id+"F1.opExtrude","SWEPT_EDGE",EDGE,{"disambiguationData":[OSD([sQuery(id+"F0.wireOp",EDGE,"E1"),sQuery(id+"F0.wireOp",EDGE,"E64.MirrorCS")])]});
            var Q125;
            Q125=makeQuery(id+"F1.opExtrude","SWEPT_EDGE",EDGE,{"disambiguationData":[OSD([sQuery(id+"F0.wireOp",EDGE,"E0"),sQuery(id+"F0.wireOp",EDGE,"E64.MirrorCS")])]});
            var Q126;
            Q126=makeQuery(id+"F1.opExtrude","SWEPT_EDGE",EDGE,{"disambiguationData":[OSD([sQuery(id+"F0.wireOp",EDGE,"E0"),sQuery(id+"F0.wireOp",EDGE,"E61.MirrorCS")])]});
            var Q127;
            Q127=makeQuery(id+"F1.opExtrude","SWEPT_EDGE",EDGE,{"disambiguationData":[OSD([sQuery(id+"F0.wireOp",EDGE,"E0"),sQuery(id+"F0.wireOp",EDGE,"E63.MirrorCS")])]});
            var Q128;
            Q128=makeQuery(id+"F1.opExtrude","SWEPT_EDGE",EDGE,{"disambiguationData":[OSD([sQuery(id+"F0.wireOp",EDGE,"E1"),sQuery(id+"F0.wireOp",EDGE,"E66.MirrorCS")])]});
            var Q129;
            Q129=makeQuery(id+"F1.opExtrude","SWEPT_EDGE",EDGE,{"disambiguationData":[OSD([sQuery(id+"F0.wireOp",EDGE,"E0"),sQuery(id+"F0.wireOp",EDGE,"E65.MirrorCS")])]});
            var Q130;
            Q130=makeQuery(id+"F1.opExtrude","SWEPT_EDGE",EDGE,{"disambiguationData":[OSD([sQuery(id+"F0.wireOp",EDGE,"E1"),sQuery(id+"F0.wireOp",EDGE,"E65.MirrorCS")])]});
            var Q131;
            Q131=makeQuery(id+"F1.opExtrude","SWEPT_EDGE",EDGE,{"disambiguationData":[OSD([sQuery(id+"F0.wireOp",EDGE,"E0"),sQuery(id+"F0.wireOp",EDGE,"E66.MirrorCS")])]});
            var Q132;
            Q132=makeQuery(id+"F1.opExtrude","SWEPT_EDGE",EDGE,{"disambiguationData":[OSD([sQuery(id+"F0.wireOp",EDGE,"E1"),sQuery(id+"F0.wireOp",EDGE,"E67.MirrorCS")])]});
            var Q133;
            Q133=makeQuery(id+"F1.opExtrude","SWEPT_EDGE",EDGE,{"disambiguationData":[OSD([sQuery(id+"F0.wireOp",EDGE,"E1"),sQuery(id+"F0.wireOp",EDGE,"E68.MirrorCS")])]});
            var Q134;
            Q134=makeQuery(id+"F1.opExtrude","SWEPT_EDGE",EDGE,{"disambiguationData":[OSD([sQuery(id+"F0.wireOp",EDGE,"E0"),sQuery(id+"F0.wireOp",EDGE,"E68.MirrorCS")])]});
            var Q135;
            Q135=makeQuery(id+"F1.opExtrude","SWEPT_EDGE",EDGE,{"disambiguationData":[OSD([sQuery(id+"F0.wireOp",EDGE,"E0"),sQuery(id+"F0.wireOp",EDGE,"E67.MirrorCS")])]});
            var Q136;
            Q136=makeQuery(id+"F1.opExtrude","SWEPT_EDGE",EDGE,{"disambiguationData":[OSD([sQuery(id+"F0.wireOp",EDGE,"E0"),sQuery(id+"F0.wireOp",EDGE,"E69.MirrorCS")])]});
            var Q137;
            Q137=makeQuery(id+"F1.opExtrude","SWEPT_EDGE",EDGE,{"disambiguationData":[OSD([sQuery(id+"F0.wireOp",EDGE,"E1"),sQuery(id+"F0.wireOp",EDGE,"E69.MirrorCS")])]});
            var Q138;
            Q138=makeQuery(id+"F1.opExtrude","SWEPT_EDGE",EDGE,{"disambiguationData":[OSD([sQuery(id+"F0.wireOp",EDGE,"E1"),sQuery(id+"F0.wireOp",EDGE,"E70.MirrorCS")])]});
            var Q139;
            Q139=makeQuery(id+"F1.opExtrude","SWEPT_EDGE",EDGE,{"disambiguationData":[OSD([sQuery(id+"F0.wireOp",EDGE,"E0"),sQuery(id+"F0.wireOp",EDGE,"E71.MirrorCS")])]});
            var Q140;
            Q140=makeQuery(id+"F1.opExtrude","SWEPT_EDGE",EDGE,{"disambiguationData":[OSD([sQuery(id+"F0.wireOp",EDGE,"E1"),sQuery(id+"F0.wireOp",EDGE,"E71.MirrorCS")])]});
            var Q141;
            Q141=makeQuery(id+"F1.opExtrude","SWEPT_EDGE",EDGE,{"disambiguationData":[OSD([sQuery(id+"F0.wireOp",EDGE,"E1"),sQuery(id+"F0.wireOp",EDGE,"E71.MirrorCS")])]});
            var Q142;
            Q142=makeQuery(id+"F1.opExtrude","SWEPT_EDGE",EDGE,{"disambiguationData":[OSD([sQuery(id+"F0.wireOp",EDGE,"E0"),sQuery(id+"F0.wireOp",EDGE,"E70.MirrorCS")])]});
            var Q143;
            Q143=makeQuery(id+"F1.opExtrude","SWEPT_EDGE",EDGE,{"disambiguationData":[OSD([sQuery(id+"F0.wireOp",EDGE,"E0"),sQuery(id+"F0.wireOp",EDGE,"E72.MirrorCS")])]});
            fillet(context, id + "F2", {"entities" : qUnion([Q0, Q1, Q2, Q3, Q4, Q5, Q6, Q7, Q8, Q9, Q10, Q11, Q12, Q13, Q14, Q15, Q16, Q17, Q18, Q19, Q20, Q21, Q22, Q23, Q24, Q25, Q26, Q27, Q28, Q29, Q30, Q31, Q32, Q33, Q34, Q35, Q36, Q37, Q38, Q39, Q40, Q41, Q42, Q43, Q44, Q45, Q46, Q47, Q48, Q49, Q50, Q51, Q52, Q53, Q54, Q55, Q56, Q57, Q58, Q59, Q60, Q61, Q62, Q63, Q64, Q65, Q66, Q67, Q68, Q69, Q70, Q71, Q72, Q73, Q74, Q75, Q76, Q77, Q78, Q79, Q80, Q81, Q82, Q83, Q84, Q85, Q86, Q87, Q88, Q89, Q90, Q91, Q92, Q93, Q94, Q95, Q96, Q97, Q98, Q99, Q100, Q101, Q102, Q103, Q104, Q105, Q106, Q107, Q108, Q109, Q110, Q111, Q112, Q113, Q114, Q115, Q116, Q117, Q118, Q119, Q120, Q121, Q122, Q123, Q124, Q125, Q126, Q127, Q128, Q129, Q130, Q131, Q132, Q133, Q134, Q135, Q136, Q137, Q138, Q139, Q140, Q141, Q142, Q143]), "radius" : 0.3 * mm, "tangentPropagation" : true, "allowEdgeOverflow" : false});
        }
    });
